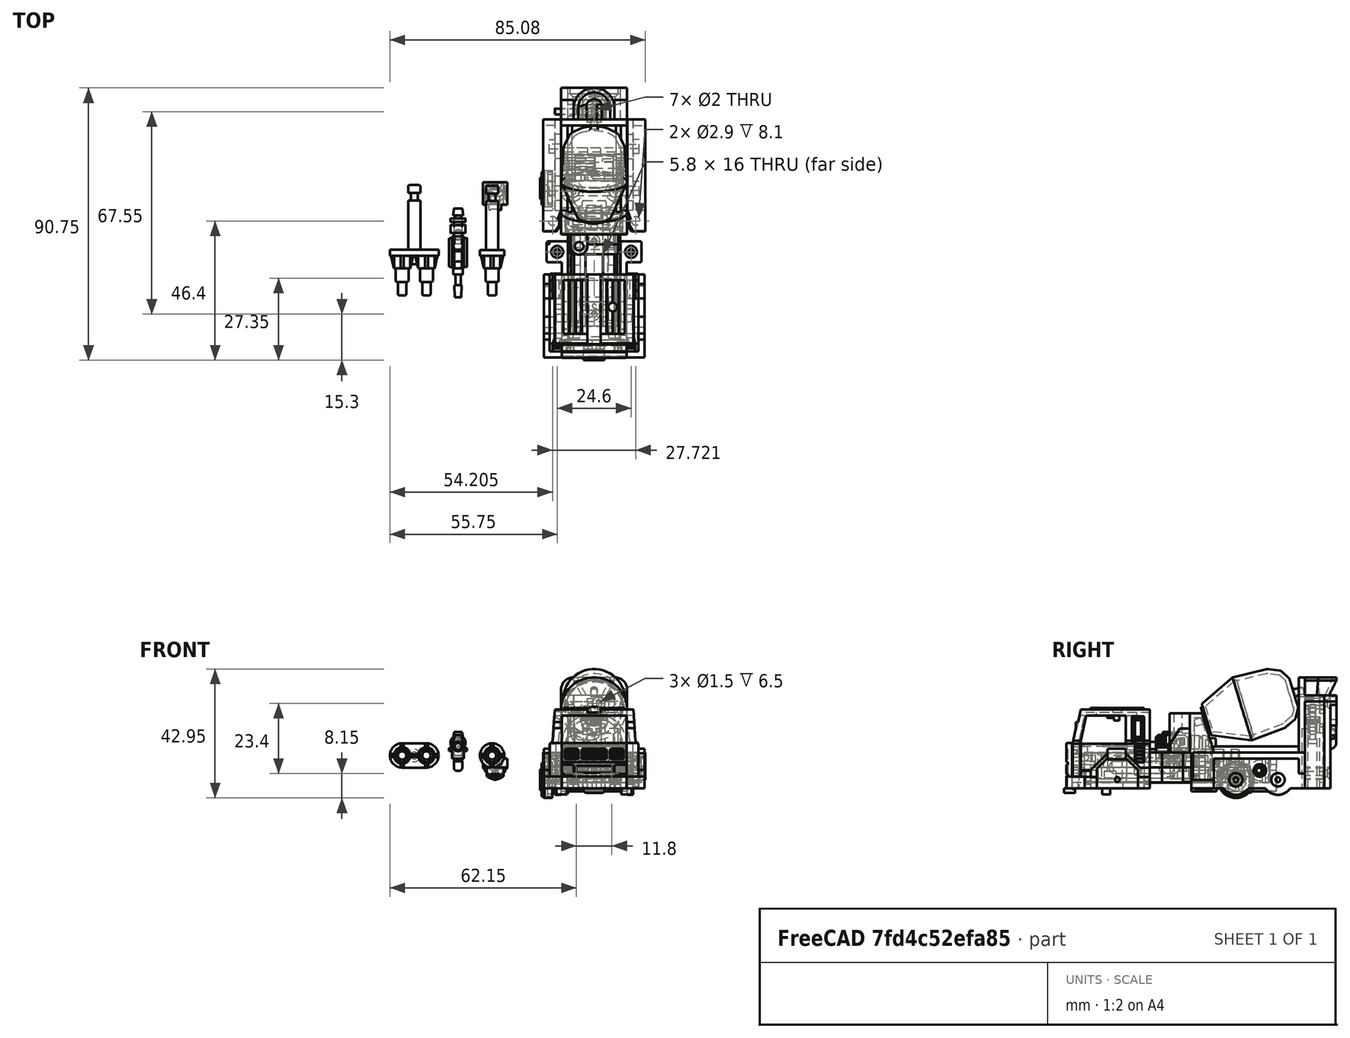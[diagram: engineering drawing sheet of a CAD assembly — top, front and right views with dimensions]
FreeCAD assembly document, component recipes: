
FREECAD ASSEMBLY — COMPONENT RECIPES ("MixMaster")

This assembly document has 25 components, labeled P0..P24 below (a component is one placed body or linked part). 24 of them carry a construction recipe — the FreeCAD feature program that regenerates the part from scratch, quoted from this document or its linked companion documents; the rest are supplied as boundary geometry only. No exploded tour is included for this assembly.
NOTE — this tour is split across 4 documents so each fits a 32k-token context. This is document 1: the component sections continue in the remaining 3 documents, each repeating the header above.
COMPONENT P0 — recipe-attached ("Rear_Torso", modeled in this document).
Construction recipe (the document's own serialized feature program — sketch geometry with constraints, then the solid features built on it; lengths are millimeters unless a unit is written):

FEATURE [Sketcher::SketchObject] Sketch
  ArcFitTolerance = 1e-06
  AttachmentSupport = -> [YZ_Plane]
  FullyConstrained = true
  MakeInternals = false
  MapMode = 5
  Placement = pos=(0,0,0) rot=(0.57735,0.57735,0.57735;2.0944rad)
  sketch-geometry (4):
    g0: LineSegment StartX=-14.5 StartY=1 StartZ=0 EndX=-14.5 EndY=-1 EndZ=0
    g1: LineSegment StartX=-14.5 StartY=-1 StartZ=0 EndX=14.5 EndY=-1 EndZ=0
    g2: LineSegment StartX=14.5 StartY=-1 StartZ=0 EndX=14.5 EndY=1 EndZ=0
    g3: LineSegment StartX=14.5 StartY=1 StartZ=0 EndX=-14.5 EndY=1 EndZ=0
  constraints (12):
    c: Coincident(g0,g1)
    c: Coincident(g1,g2)
    c: Coincident(g2,g3)
    c: Coincident(g3,g0)
    c: Vertical(g0)
    c: Vertical(g2)
    c: Horizontal(g1)
    c: Horizontal(g3)
    c: DistanceX(g3,g3) = 29
    c: DistanceY(g0,g0) = 2
    c: DistanceY(g-1,g0) = 1
    c: DistanceX(g0,g-1) = 14.5
FEATURE [PartDesign::Pad] Pad
  Direction = (1,0,0)
  Length = 22
  Length2 = 10
  Placement = pos=(0,0,0) rot=(1,1,1;2.0944rad)
  Profile = -> Sketch
  ReferenceAxis = -> Sketch [N_Axis]
  Refine = true
  Suppressed = false
  Type = 0
FEATURE [Sketcher::SketchObject] Sketch001
  ArcFitTolerance = 1e-06
  AttachmentSupport = -> [Pad]
  ExternalGeometry = -> [Pad]
  FullyConstrained = true
  MakeInternals = false
  MapMode = 5
  Placement = pos=(22,0,0) rot=(0.57735,0.57735,0.57735;2.0944rad)
  sketch-geometry (4):
    g0: LineSegment StartX=-14.5 StartY=1 StartZ=0 EndX=-21.3 EndY=1 EndZ=0
    g1: LineSegment StartX=-21.3 StartY=1 StartZ=0 EndX=-21.3 EndY=-6 EndZ=0
    g2: LineSegment StartX=-21.3 StartY=-6 StartZ=0 EndX=-14.5 EndY=-6 EndZ=0
    g3: LineSegment StartX=-14.5 StartY=-6 StartZ=0 EndX=-14.5 EndY=1 EndZ=0
  constraints (11):
    c: Coincident(g0,g1)
    c: Coincident(g1,g2)
    c: Coincident(g2,g3)
    c: Coincident(g3,g0)
    c: Horizontal(g0)
    c: Horizontal(g2)
    c: Vertical(g1)
    c: Vertical(g3)
    c: Coincident(g0,g-3)
    c: DistanceX(g0,g0) = 6.8
    c: DistanceY(g1,g1) = 7
FEATURE [PartDesign::Pad] Pad001
  BaseFeature = -> Pad
  Direction = (1,0,0)
  Length = 1.5
  Length2 = 10
  Placement = pos=(0,0,0) rot=(1,1,1;2.0944rad)
  Profile = -> Sketch001
  ReferenceAxis = -> Sketch001 [N_Axis]
  Refine = true
  Reversed = true
  Suppressed = false
  Type = 0
FEATURE [Sketcher::SketchObject] Sketch002
  ArcFitTolerance = 1e-06
  AttachmentSupport = -> [Pad001]
  ExternalGeometry = -> [Pad001]
  FullyConstrained = true
  MakeInternals = false
  MapMode = 5
  Placement = pos=(22,0,0) rot=(0.57735,0.57735,0.57735;2.0944rad)
  sketch-geometry (4):
    g0: LineSegment StartX=-21.8 StartY=1 StartZ=0 EndX=-13.8 EndY=1 EndZ=0
    g1: LineSegment StartX=-13.8 StartY=1 StartZ=0 EndX=-17.8 EndY=14.1 EndZ=0
    g2: LineSegment StartX=-17.8 StartY=14.1 StartZ=0 EndX=-21.8 EndY=14.1 EndZ=0
    g3: LineSegment StartX=-21.8 StartY=14.1 StartZ=0 EndX=-21.8 EndY=1 EndZ=0
  constraints (12):
    c: Coincident(g0,g1)
    c: Coincident(g1,g2)
    c: Coincident(g2,g3)
    c: Horizontal(g0)
    c: Horizontal(g2)
    c: DistanceY(g3,g3) = 13.1
    c: DistanceX(g0,g0) = 8
    c: Coincident(g0,g3)
    c: Vertical(g3)
    c: DistanceX(g0,g-3) = 0.5
    c: DistanceX(g2,g2) = 4
    c: PointOnObject(g-3,g0)
FEATURE [PartDesign::Pad] Pad002
  BaseFeature = -> Pad001
  Direction = (1,0,0)
  Length = 22
  Length2 = 10
  Placement = pos=(0,0,0) rot=(1,1,1;2.0944rad)
  Profile = -> Sketch002
  ReferenceAxis = -> Sketch002 [N_Axis]
  Refine = true
  Reversed = true
  Suppressed = false
  Type = 0
FEATURE [Sketcher::SketchObject] Sketch003
  ArcFitTolerance = 1e-06
  AttachmentSupport = -> [Pad002]
  ExternalGeometry = -> [Pad002]
  FullyConstrained = true
  MakeInternals = false
  MapMode = 5
  Placement = pos=(8e-16,0,0) rot=(0.57735,0.57735,-0.57735;4.18879rad)
  sketch-geometry (4):
    g0: LineSegment StartX=-14.5 StartY=-1 StartZ=0 EndX=-14.5 EndY=6 EndZ=0
    g1: LineSegment StartX=-14.5 StartY=6 StartZ=0 EndX=-21.3 EndY=6 EndZ=0
    g2: LineSegment StartX=-21.3 StartY=6 StartZ=0 EndX=-21.3 EndY=-1 EndZ=0
    g3: LineSegment StartX=-21.3 StartY=-1 StartZ=0 EndX=-14.5 EndY=-1 EndZ=0
  constraints (11):
    c: Coincident(g0,g1)
    c: Coincident(g1,g2)
    c: Coincident(g2,g3)
    c: Coincident(g3,g0)
    c: Vertical(g0)
    c: Vertical(g2)
    c: Horizontal(g1)
    c: Horizontal(g3)
    c: Coincident(g0,g-4)
    c: DistanceX(g1,g1) = 6.8
    c: DistanceY(g0,g0) = 7
FEATURE [PartDesign::Pad] Pad003
  BaseFeature = -> Pad002
  Direction = (-1,0,0)
  Length = 1.5
  Length2 = 10
  Placement = pos=(0,0,0) rot=(1,1,1;2.0944rad)
  Profile = -> Sketch003
  ReferenceAxis = -> Sketch003 [N_Axis]
  Refine = true
  Reversed = true
  Suppressed = false
  Type = 0
FEATURE [Sketcher::SketchObject] Sketch004
  ArcFitTolerance = 1e-06
  AttachmentSupport = -> [Pad003]
  ExternalGeometry = -> [Pad003]
  FullyConstrained = true
  MakeInternals = false
  MapMode = 5
  Placement = pos=(-4.8e-15,-21.8,0) rot=(0.57735,0.57735,-0.57735;2.0944rad)
  sketch-geometry (4):
    g0: ArcOfCircle CenterX=-3.1 CenterY=11 CenterZ=0 NormalX=0 NormalY=0 NormalZ=1 AngleXU=0 Radius=11 StartAngle=1.5708 EndAngle=4.71239
    g1: LineSegment StartX=-3.1 StartY=22 StartZ=0 EndX=-14.1 EndY=22 EndZ=0
    g2: LineSegment StartX=-14.1 StartY=22 StartZ=0 EndX=-14.1 EndY=0 EndZ=0
    g3: LineSegment StartX=-14.1 StartY=0 StartZ=0 EndX=-3.1 EndY=0 EndZ=0
  constraints (10):
    c: PointOnObject(g0,g-1)
    c: PointOnObject(g0,g-3)
    c: DistanceX(g0,g0) = 0
    c: DistanceX(g0,g-5) = 2.1
    c: Tangent(g1,g0) = -1.5708
    c: Coincident(g1,g-4)
    c: Coincident(g2,g1)
    c: Coincident(g2,g-4)
    c: Coincident(g3,g2)
    c: Coincident(g3,g0)
FEATURE [PartDesign::Pocket] Pocket
  BaseFeature = -> Pad003
  Direction = (0,1,0)
  Length = 8
  Length2 = 5
  Placement = pos=(0,0,0) rot=(1,1,1;2.0944rad)
  Profile = -> Sketch004
  ReferenceAxis = -> Sketch004 [N_Axis]
  Refine = true
  Suppressed = false
  Type = 0
FEATURE [Sketcher::SketchObject] Sketch005
  ArcFitTolerance = 1e-06
  AttachmentSupport = -> [Pocket]
  ExternalGeometry = -> [Pocket]
  FullyConstrained = true
  MakeInternals = false
  MapMode = 5
  Placement = pos=(-4.8e-15,-21.8,0) rot=(0.57735,0.57735,-0.57735;2.0944rad)
  sketch-geometry (4):
    g0: ArcOfCircle CenterX=-3.1 CenterY=11 CenterZ=0 NormalX=0 NormalY=0 NormalZ=1 AngleXU=0 Radius=9.5 StartAngle=1.5708 EndAngle=4.71239
    g1: LineSegment StartX=-3.1 StartY=20.5 StartZ=0 EndX=-1 EndY=20.5 EndZ=0
    g2: LineSegment StartX=-3.1 StartY=1.5 StartZ=0 EndX=-1 EndY=1.5 EndZ=0
    g3: LineSegment StartX=-1 StartY=20.5 StartZ=0 EndX=-1 EndY=1.5 EndZ=0
  constraints (12):
    c: Coincident(g0,g-3)
    c: Radius(g0) = 9.5
    c: Coincident(g1,g0)
    c: PointOnObject(g1,g-4)
    c: Horizontal(g1)
    c: Coincident(g2,g0)
    c: PointOnObject(g2,g-4)
    c: Horizontal(g2)
    c: DistanceY(g0,g-5) = 1.5
    c: DistanceX(g0,g0) = 0
    c: Coincident(g3,g1)
    c: Coincident(g3,g2)
FEATURE [Sketcher::SketchObject] Sketch006
  ArcFitTolerance = 1e-06
  FullyConstrained = true
  MakeInternals = false
  MapMode = 5
  Placement = pos=(1.4e-15,-12.3438,-3.7691) rot=(-0.511311,-0.511311,-0.690741;1.93262rad)
  sketch-geometry (4):
    g0: ArcOfCircle CenterX=7.18218 CenterY=11 CenterZ=0 NormalX=0 NormalY=0 NormalZ=1 AngleXU=0 Radius=9.5 StartAngle=4.71239 EndAngle=7.85398
    g1: LineSegment StartX=7.18218 StartY=1.5 StartZ=0 EndX=4.98646 EndY=1.5 EndZ=0
    g2: LineSegment StartX=7.18218 StartY=20.5 StartZ=0 EndX=4.98646 EndY=20.5 EndZ=0
    g3: LineSegment StartX=4.98646 StartY=20.5 StartZ=0 EndX=4.98646 EndY=1.5 EndZ=0
  constraints (12):
    c: Coincident(g0,g-3)
    c: Radius(g0) = 9.5
    c: Coincident(g1,g0)
    c: PointOnObject(g1,g-5)
    c: Horizontal(g1)
    c: Coincident(g2,g0)
    c: PointOnObject(g2,g-5)
    c: Horizontal(g2)
    c: Coincident(g3,g2)
    c: Coincident(g3,g1)
    c: DistanceX(g0,g0) = 0
    c: DistanceX(g0,g0) = 0
FEATURE [PartDesign::Pocket] Pocket002
  BaseFeature = -> Pocket
  Direction = (-1e-16,-0.956408,-0.292033)
  Length = 8
  Length2 = 5
  Placement = pos=(0,0,0) rot=(1,1,1;2.0944rad)
  Profile = -> Sketch006
  ReferenceAxis = -> Sketch006 [N_Axis]
  Refine = true
  Suppressed = false
  Type = 0
FEATURE [PartDesign::Pocket] Pocket003
  BaseFeature = -> Pocket002
  Direction = (0,1,0)
  Length = 8
  Length2 = 5
  Placement = pos=(0,0,0) rot=(1,1,1;2.0944rad)
  Profile = -> Sketch005
  ReferenceAxis = -> Sketch005 [N_Axis]
  Refine = true
  Suppressed = false
  Type = 0
FEATURE [Sketcher::SketchObject] Sketch007
  ArcFitTolerance = 1e-06
  AttachmentSupport = -> [Pocket003]
  ExternalGeometry = -> [Pocket003]
  FullyConstrained = true
  MakeInternals = false
  MapMode = 5
  Placement = pos=(-2.7e-15,-12.3438,-3.7691) rot=(-0.511311,-0.511311,-0.690741;1.93262rad)
  sketch-geometry (4):
    g0: LineSegment StartX=7.18218 StartY=21 StartZ=0 EndX=4.98646 EndY=21 EndZ=0
    g1: LineSegment StartX=4.98646 StartY=21 StartZ=0 EndX=4.98646 EndY=1 EndZ=0
    g2: LineSegment StartX=4.98646 StartY=1 StartZ=0 EndX=7.18218 EndY=1 EndZ=0
    g3: ArcOfCircle CenterX=7.18218 CenterY=11 CenterZ=0 NormalX=0 NormalY=0 NormalZ=1 AngleXU=0 Radius=10 StartAngle=4.71239 EndAngle=7.85398
  constraints (12):
    c: Vertical(g1)
    c: Horizontal(g2)
    c: PointOnObject(g2,g-6)
    c: Coincident(g2,g3)
    c: Coincident(g0,g3)
    c: Horizontal(g0)
    c: Radius(g3) = 10
    c: Coincident(g-3,g3)
    c: DistanceX(g0,g3) = 0
    c: DistanceX(g2,g3) = 0
    c: Coincident(g1,g2)
    c: Coincident(g1,g0)
FEATURE [PartDesign::Pad] Pad004
  BaseFeature = -> Pocket003
  Direction = (0,0.956408,0.292033)
  Length = 0.734
  Length2 = 10
  Placement = pos=(0,0,0) rot=(1,1,1;2.0944rad)
  Profile = -> Sketch007
  ReferenceAxis = -> Sketch007 [N_Axis]
  Refine = true
  Reversed = true
  Suppressed = false
  Type = 0
FEATURE [Sketcher::SketchObject] Sketch008
  ArcFitTolerance = 1e-06
  AttachmentSupport = -> [Pad004]
  ExternalGeometry = -> [Pad004]
  FullyConstrained = true
  MakeInternals = false
  MapMode = 5
  Placement = pos=(22,0,1.47e-14) rot=(0.57735,0.57735,0.57735;2.0944rad)
  sketch-geometry (4):
    g0: LineSegment StartX=14.5 StartY=26 StartZ=0 EndX=14.5 EndY=-11 EndZ=0
    g1: LineSegment StartX=14.5 StartY=-11 StartZ=0 EndX=16.5 EndY=-11 EndZ=0
    g2: LineSegment StartX=16.5 StartY=-11 StartZ=0 EndX=16.5 EndY=26 EndZ=0
    g3: LineSegment StartX=16.5 StartY=26 StartZ=0 EndX=14.5 EndY=26 EndZ=0
  constraints (12):
    c: Coincident(g0,g1)
    c: Coincident(g1,g2)
    c: Coincident(g2,g3)
    c: Coincident(g3,g0)
    c: Vertical(g0)
    c: Vertical(g2)
    c: Horizontal(g1)
    c: Horizontal(g3)
    c: DistanceY(g2,g2) = 37
    c: DistanceX(g3,g3) = 2
    c: PointOnObject(g-3,g0)
    c: DistanceY(g0,g-3) = 10
FEATURE [PartDesign::Pad] Pad005
  BaseFeature = -> Pad004
  Direction = (1,-1e-15,1.2e-15)
  Length = 22
  Length2 = 10
  Placement = pos=(0,0,0) rot=(1,1,1;2.0944rad)
  Profile = -> Sketch008
  ReferenceAxis = -> Sketch008 [N_Axis]
  Refine = true
  Reversed = true
  Suppressed = false
  Type = 0
FEATURE [Sketcher::SketchObject] Sketch009
  ArcFitTolerance = 1e-06
  AttachmentSupport = -> [Pad005]
  ExternalGeometry = -> [Pad005]
  FullyConstrained = true
  MakeInternals = false
  MapMode = 5
  Placement = pos=(-1.21e-14,-12.3438,-3.7691) rot=(-0.511311,-0.511311,-0.690741;1.93262rad)
  sketch-geometry (4):
    g0: LineSegment StartX=14.4865 StartY=12.3 StartZ=0 EndX=14.4865 EndY=9.7 EndZ=0
    g1: LineSegment StartX=14.4865 StartY=9.7 StartZ=0 EndX=17.0865 EndY=9.7 EndZ=0
    g2: LineSegment StartX=17.0865 StartY=9.7 StartZ=0 EndX=17.0865 EndY=12.3 EndZ=0
    g3: LineSegment StartX=17.0865 StartY=12.3 StartZ=0 EndX=14.4865 EndY=12.3 EndZ=0
  constraints (12):
    c: Coincident(g0,g1)
    c: Coincident(g1,g2)
    c: Coincident(g2,g3)
    c: Coincident(g3,g0)
    c: Vertical(g0)
    c: Vertical(g2)
    c: Horizontal(g1)
    c: Horizontal(g3)
    c: DistanceX(g3,g3) = 2.6
    c: DistanceY(g0,g0) = 2.6
    c: DistanceX(g-3,g0) = 9.5
    c: DistanceY(g0,g-3) = 9.7
FEATURE [PartDesign::Pocket] Pocket004
  BaseFeature = -> Pad005
  Direction = (0,-0.956408,-0.292033)
  Length = 1
  Length2 = 5
  Placement = pos=(0,0,0) rot=(1,1,1;2.0944rad)
  Profile = -> Sketch009
  ReferenceAxis = -> Sketch009 [N_Axis]
  Refine = true
  Suppressed = false
  Type = 0
FEATURE [Sketcher::SketchObject] Sketch010
  ArcFitTolerance = 1e-06
  AttachmentSupport = -> [Pocket004]
  ExternalGeometry = -> [Pocket004]
  FullyConstrained = true
  MakeInternals = false
  MapMode = 5
  Placement = pos=(0,5e-16,1) rot=(0,0,-1;1.5708rad)
  sketch-geometry (8):
    g0: LineSegment StartX=-14.5 StartY=19.9 StartZ=0 EndX=-14.5 EndY=18.3 EndZ=0
    g1: LineSegment StartX=-14.5 StartY=18.3 StartZ=0 EndX=14.502 EndY=18.3 EndZ=0
    g2: LineSegment StartX=14.502 StartY=18.3 StartZ=0 EndX=14.502 EndY=19.9 EndZ=0
    g3: LineSegment StartX=14.502 StartY=19.9 StartZ=0 EndX=-14.5 EndY=19.9 EndZ=0
    g4: LineSegment StartX=-14.5 StartY=3.7 StartZ=0 EndX=-14.5 EndY=2.1 EndZ=0
    g5: LineSegment StartX=-14.5 StartY=2.1 StartZ=0 EndX=14.502 EndY=2.1 EndZ=0
    g6: LineSegment StartX=14.502 StartY=2.1 StartZ=0 EndX=14.502 EndY=3.7 EndZ=0
    g7: LineSegment StartX=14.502 StartY=3.7 StartZ=0 EndX=-14.5 EndY=3.7 EndZ=0
  constraints (24):
    c: Coincident(g0,g1)
    c: Coincident(g1,g2)
    c: Coincident(g2,g3)
    c: Coincident(g3,g0)
    c: Vertical(g0)
    c: Horizontal(g1)
    c: Horizontal(g3)
    c: PointOnObject(g0,g-4)
    c: Coincident(g4,g5)
    c: Coincident(g5,g6)
    c: Coincident(g7,g4)
    c: Vertical(g4)
    c: Horizontal(g5)
    c: Horizontal(g7)
    c: PointOnObject(g4,g-4)
    c: DistanceY(g4,g4) = 1.6
    c: DistanceY(g0,g0) = 1.6
    c: DistanceY(g0,g-5) = 2.1
    c: DistanceY(g-6,g4) = 2.1
    c: PointOnObject(g7,g-7)
    c: Coincident(g6,g7)
    c: PointOnObject(g5,g-7)
    c: PointOnObject(g2,g-7)
    c: PointOnObject(g1,g-7)
FEATURE [PartDesign::Pad] Pad006
  BaseFeature = -> Pocket004
  Direction = (-2.8e-15,1.5e-15,1)
  Length = 2
  Length2 = 10
  Placement = pos=(0,0,0) rot=(1,1,1;2.0944rad)
  Profile = -> Sketch010
  ReferenceAxis = -> Sketch010 [N_Axis]
  Refine = true
  Suppressed = false
  Type = 0
FEATURE [Sketcher::SketchObject] Sketch011
  ArcFitTolerance = 1e-06
  AttachmentSupport = -> [Pad006]
  ExternalGeometry = -> [Pad006]
  FullyConstrained = true
  MakeInternals = false
  MapMode = 5
  Placement = pos=(1.77e-14,14.5,1.6e-15) rot=(0.57735,0.57735,-0.57735;2.0944rad)
  sketch-geometry (6):
    g0: LineSegment StartX=-26 StartY=22 StartZ=0 EndX=-22 EndY=22 EndZ=0
    g1: LineSegment StartX=-26 StartY=22 StartZ=0 EndX=-26 EndY=18 EndZ=0
    g2: ArcOfCircle CenterX=-22 CenterY=18 CenterZ=0 NormalX=0 NormalY=0 NormalZ=1 AngleXU=0 Radius=4 StartAngle=1.5708 EndAngle=3.14159
    g3: LineSegment StartX=-26 StartY=0 StartZ=0 EndX=-26 EndY=4 EndZ=0
    g4: LineSegment StartX=-26 StartY=0 StartZ=0 EndX=-22 EndY=-4e-15 EndZ=0
    g5: ArcOfCircle CenterX=-22 CenterY=4 CenterZ=0 NormalX=0 NormalY=0 NormalZ=1 AngleXU=0 Radius=4 StartAngle=3.14159 EndAngle=4.71239
  constraints (18):
    c: Coincident(g0,g-4)
    c: PointOnObject(g0,g-3)
    c: Coincident(g1,g0)
    c: PointOnObject(g1,g-4)
    c: Coincident(g2,g1)
    c: Coincident(g2,g0)
    c: Coincident(g3,g-5)
    c: PointOnObject(g3,g-4)
    c: Coincident(g4,g3)
    c: PointOnObject(g4,g-5)
    c: Coincident(g5,g4)
    c: Coincident(g5,g3)
    c: Radius(g5) = 4
    c: Radius(g2) = 4
    c: DistanceX(g5,g4) = 0
    c: DistanceX(g0,g2) = 0
    c: DistanceY(g1,g2) = 0
    c: DistanceY(g3,g5) = 0
FEATURE [PartDesign::Pocket] Pocket005
  BaseFeature = -> Pad006
  Direction = (1.3e-15,1,0)
  Length = 2
  Length2 = 5
  Placement = pos=(0,0,0) rot=(1,1,1;2.0944rad)
  Profile = -> Sketch011
  ReferenceAxis = -> Sketch011 [N_Axis]
  Refine = true
  Suppressed = false
  Type = 0
FEATURE [Sketcher::SketchObject] Sketch012
  ArcFitTolerance = 1e-06
  AttachmentSupport = -> [Pocket005]
  ExternalGeometry = -> [Pocket005]
  FullyConstrained = true
  MakeInternals = false
  MapMode = 5
  Placement = pos=(1.77e-14,14.5,1.6e-15) rot=(0.57735,0.57735,-0.57735;2.0944rad)
  sketch-geometry (4):
    g0: LineSegment StartX=-21.9 StartY=12.1 StartZ=0 EndX=-21.9 EndY=9.9 EndZ=0
    g1: LineSegment StartX=-21.9 StartY=9.9 StartZ=0 EndX=-19.1 EndY=9.9 EndZ=0
    g2: LineSegment StartX=-19.1 StartY=9.9 StartZ=0 EndX=-19.1 EndY=12.1 EndZ=0
    g3: LineSegment StartX=-19.1 StartY=12.1 StartZ=0 EndX=-21.9 EndY=12.1 EndZ=0
  constraints (12):
    c: Coincident(g0,g1)
    c: Coincident(g1,g2)
    c: Coincident(g2,g3)
    c: Coincident(g3,g0)
    c: Vertical(g0)
    c: Vertical(g2)
    c: Horizontal(g1)
    c: Horizontal(g3)
    c: DistanceX(g3,g3) = 2.8
    c: DistanceY(g0,g0) = 2.2
    c: DistanceY(g0,g-3) = 9.9
    c: DistanceX(g-5,g0) = 4.1
FEATURE [PartDesign::Pocket] Pocket006
  BaseFeature = -> Pocket005
  Direction = (1.3e-15,1,0)
  Length = 2
  Length2 = 5
  Placement = pos=(0,0,0) rot=(1,1,1;2.0944rad)
  Profile = -> Sketch012
  ReferenceAxis = -> Sketch012 [N_Axis]
  Refine = true
  Suppressed = false
  Type = 0
FEATURE [Sketcher::SketchObject] Sketch015
  ArcFitTolerance = 1e-06
  AttachmentSupport = -> [Pocket006]
  ExternalGeometry = -> [Pocket006]
  FullyConstrained = true
  MakeInternals = false
  MapMode = 5
  Placement = pos=(-4.8e-15,-21.8,0) rot=(0.57735,0.57735,-0.57735;2.0944rad)
  sketch-geometry (4):
    g0: LineSegment StartX=-1 StartY=20.5 StartZ=0 EndX=-1 EndY=1.5 EndZ=0
    g1: LineSegment StartX=-1 StartY=1.5 StartZ=0 EndX=-3.1 EndY=1.5 EndZ=0
    g2: LineSegment StartX=-1 StartY=20.5 StartZ=0 EndX=-3.1 EndY=20.5 EndZ=0
    g3: ArcOfCircle CenterX=-3.1 CenterY=11 CenterZ=0 NormalX=0 NormalY=0 NormalZ=1 AngleXU=0 Radius=9.5 StartAngle=1.5708 EndAngle=4.71239
  constraints (9):
    c: Coincident(g0,g-3)
    c: Coincident(g0,g-4)
    c: Coincident(g1,g0)
    c: Coincident(g1,g-5)
    c: Coincident(g2,g0)
    c: Coincident(g2,g-5)
    c: Coincident(g3,g2)
    c: Coincident(g3,g1)
    c: Radius(g3) = 9.5
FEATURE [PartDesign::Pad] Pad007
  BaseFeature = -> Pocket006
  Direction = (-1e-16,-1,3.2e-15)
  Length = 1.5
  Length2 = 10
  Placement = pos=(0,0,0) rot=(1,1,1;2.0944rad)
  Profile = -> Sketch015
  ReferenceAxis = -> Sketch015 [N_Axis]
  Refine = true
  Reversed = true
  Suppressed = false
  Type = 0
FEATURE [Sketcher::SketchObject] Sketch016
  ArcFitTolerance = 1e-06
  AttachmentSupport = -> [Pad007]
  ExternalGeometry = -> [Pad007]
  FullyConstrained = true
  MakeInternals = false
  MapMode = 5
  Placement = pos=(-3.62e-14,-21.8,8.98e-14) rot=(0.57735,0.57735,-0.57735;2.0944rad)
  sketch-geometry (4):
    g0: LineSegment StartX=-1 StartY=4.5 StartZ=0 EndX=-7.5 EndY=4.5 EndZ=0
    g1: LineSegment StartX=-7.5 StartY=4.5 StartZ=0 EndX=-7.5 EndY=17.5 EndZ=0
    g2: LineSegment StartX=-7.5 StartY=17.5 StartZ=0 EndX=-1 EndY=17.5 EndZ=0
    g3: LineSegment StartX=-1 StartY=17.5 StartZ=0 EndX=-1 EndY=4.5 EndZ=0
  constraints (12):
    c: PointOnObject(g0,g-3)
    c: Horizontal(g0)
    c: Coincident(g1,g0)
    c: Vertical(g1)
    c: Coincident(g2,g1)
    c: PointOnObject(g2,g-3)
    c: Horizontal(g2)
    c: Coincident(g3,g2)
    c: Coincident(g3,g0)
    c: DistanceY(g-3,g0) = 4.5
    c: DistanceY(g2,g-3) = 4.5
    c: DistanceX(g2,g2) = 6.5
FEATURE [PartDesign::Pocket] Pocket007
  BaseFeature = -> Pad007
  Direction = (1.6e-15,1,-4.3e-15)
  Length = 1.5
  Length2 = 5
  Placement = pos=(0,0,0) rot=(1,1,1;2.0944rad)
  Profile = -> Sketch016
  ReferenceAxis = -> Sketch016 [N_Axis]
  Refine = true
  Suppressed = false
  Type = 0
FEATURE [Sketcher::SketchObject] Sketch017
  ArcFitTolerance = 1e-06
  AttachmentSupport = -> [Pocket007]
  ExternalGeometry = -> [Pocket007]
  FullyConstrained = true
  MakeInternals = false
  MapMode = 5
  Placement = pos=(-3.62e-14,-21.8,8.98e-14) rot=(0.57735,0.57735,-0.57735;2.0944rad)
  sketch-geometry (8):
    g0: LineSegment StartX=-1 StartY=4.5 StartZ=0 EndX=-7.5 EndY=4.5 EndZ=0
    g1: LineSegment StartX=-7.5 StartY=17.5 StartZ=0 EndX=-7.5 EndY=4.5 EndZ=0
    g2: LineSegment StartX=-7.5 StartY=17.5 StartZ=0 EndX=-1 EndY=17.5 EndZ=0
    g3: LineSegment StartX=-1 StartY=17.5 StartZ=0 EndX=-1 EndY=19 EndZ=0
    g4: LineSegment StartX=-1 StartY=19 StartZ=0 EndX=-9 EndY=19 EndZ=0
    g5: LineSegment StartX=-9 StartY=19 StartZ=0 EndX=-9 EndY=3 EndZ=0
    g6: LineSegment StartX=-9 StartY=3 StartZ=0 EndX=-1 EndY=3 EndZ=0
    g7: LineSegment StartX=-1 StartY=3 StartZ=0 EndX=-1 EndY=4.5 EndZ=0
  constraints (20):
    c: Coincident(g0,g-5)
    c: Coincident(g0,g-5)
    c: Coincident(g1,g-4)
    c: Coincident(g1,g0)
    c: Coincident(g2,g1)
    c: Coincident(g2,g-3)
    c: Coincident(g3,g2)
    c: Vertical(g3)
    c: Coincident(g4,g3)
    c: Horizontal(g4)
    c: Coincident(g5,g4)
    c: Vertical(g5)
    c: Coincident(g6,g5)
    c: Horizontal(g6)
    c: Coincident(g7,g6)
    c: Coincident(g7,g0)
    c: Vertical(g7)
    c: DistanceY(g3,g3) = 1.5
    c: DistanceY(g7,g7) = 1.5
    c: DistanceX(g5,g0) = 1.5
FEATURE [PartDesign::Pad] Pad008
  BaseFeature = -> Pocket007
  Direction = (-1.8e-15,-1,4.5e-15)
  Length = 3.3
  Length2 = 10
  Placement = pos=(0,0,0) rot=(1,1,1;2.0944rad)
  Profile = -> Sketch017
  ReferenceAxis = -> Sketch017 [N_Axis]
  Refine = true
  Suppressed = false
  Type = 0
FEATURE [Sketcher::SketchObject] Sketch018
  ArcFitTolerance = 1e-06
  AttachmentSupport = -> [Pad008]
  ExternalGeometry = -> [Pad008]
  FullyConstrained = true
  MakeInternals = false
  MapMode = 5
  Placement = pos=(3,-5.5e-15,-7e-16) rot=(-0.57735,-0.57735,0.57735;2.0944rad)
  sketch-geometry (4):
    g0: LineSegment StartX=-25.1 StartY=-1 StartZ=0 EndX=-25.1 EndY=-9 EndZ=0
    g1: LineSegment StartX=-25.1 StartY=-9 StartZ=0 EndX=-28.4 EndY=-4 EndZ=0
    g2: LineSegment StartX=-28.4 StartY=-4 StartZ=0 EndX=-28.4 EndY=-1 EndZ=0
    g3: LineSegment StartX=-25.1 StartY=-1 StartZ=0 EndX=-28.4 EndY=-1 EndZ=0
  constraints (10):
    c: Coincident(g0,g-3)
    c: Coincident(g0,g-3)
    c: Coincident(g1,g0)
    c: Coincident(g2,g1)
    c: Vertical(g2)
    c: Coincident(g3,g0)
    c: Horizontal(g3)
    c: Coincident(g3,g2)
    c: DistanceX(g3,g3) = 3.3
    c: DistanceY(g2,g2) = 3
FEATURE [PartDesign::Pad] Pad009
  BaseFeature = -> Pad008
  Direction = (-1,1.8e-15,0)
  Length = 1.5
  Length2 = 10
  Placement = pos=(0,0,0) rot=(1,1,1;2.0944rad)
  Profile = -> Sketch018
  ReferenceAxis = -> Sketch018 [N_Axis]
  Refine = true
  Reversed = true
  Suppressed = false
  Type = 0
FEATURE [Sketcher::SketchObject] Sketch019
  ArcFitTolerance = 1e-06
  AttachmentSupport = -> [Pad009]
  ExternalGeometry = -> [Pad009]
  FullyConstrained = true
  MakeInternals = false
  MapMode = 5
  Placement = pos=(19,-3.48e-14,-4.2e-15) rot=(0.57735,0.57735,0.57735;2.0944rad)
  sketch-geometry (4):
    g0: LineSegment StartX=-25.1 StartY=9 StartZ=0 EndX=-25.1 EndY=1 EndZ=0
    g1: LineSegment StartX=-25.1 StartY=1 StartZ=0 EndX=-28.4 EndY=1 EndZ=0
    g2: LineSegment StartX=-28.4 StartY=1 StartZ=0 EndX=-28.4 EndY=4 EndZ=0
    g3: LineSegment StartX=-28.4 StartY=4 StartZ=0 EndX=-25.1 EndY=9 EndZ=0
  constraints (10):
    c: Coincident(g0,g-3)
    c: Coincident(g0,g-3)
    c: Coincident(g1,g0)
    c: Horizontal(g1)
    c: Coincident(g2,g1)
    c: Vertical(g2)
    c: Coincident(g3,g2)
    c: Coincident(g3,g0)
    c: DistanceX(g1,g1) = 3.3
    c: DistanceY(g2,g2) = 3
FEATURE [PartDesign::Pad] Pad010
  BaseFeature = -> Pad009
  Direction = (1,-1.9e-15,-1e-16)
  Length = 1.5
  Length2 = 10
  Placement = pos=(0,0,0) rot=(1,1,1;2.0944rad)
  Profile = -> Sketch019
  ReferenceAxis = -> Sketch019 [N_Axis]
  Refine = true
  Reversed = true
  Suppressed = false
  Type = 0
FEATURE [Sketcher::SketchObject] Sketch020
  ArcFitTolerance = 1e-06
  AttachmentSupport = -> [Pad010]
  ExternalGeometry = -> [Pad010]
  FullyConstrained = true
  MakeInternals = false
  MapMode = 5
  Placement = pos=(-4.33e-14,-21.6216,14.2703) rot=(0.428244,0.428244,-0.795748;1.79731rad)
  sketch-geometry (4):
    g0: LineSegment StartX=12.3055 StartY=17.5 StartZ=0 EndX=6.31465 EndY=17.5 EndZ=0
    g1: LineSegment StartX=6.31465 StartY=17.5 StartZ=0 EndX=6.31465 EndY=4.5 EndZ=0
    g2: LineSegment StartX=6.31465 StartY=4.5 StartZ=0 EndX=12.3055 EndY=4.5 EndZ=0
    g3: LineSegment StartX=12.3055 StartY=4.5 StartZ=0 EndX=12.3055 EndY=17.5 EndZ=0
  constraints (8):
    c: Coincident(g0,g-3)
    c: Coincident(g0,g-4)
    c: Coincident(g1,g0)
    c: Coincident(g1,g-5)
    c: Coincident(g2,g1)
    c: Coincident(g2,g-5)
    c: Coincident(g3,g2)
    c: Coincident(g3,g0)
FEATURE [PartDesign::Pad] Pad011
  BaseFeature = -> Pad010
  Direction = (-1.9e-15,-0.834609,0.550842)
  Length = 1.5
  Length2 = 10
  Placement = pos=(0,0,0) rot=(1,1,1;2.0944rad)
  Profile = -> Sketch020
  ReferenceAxis = -> Sketch020 [N_Axis]
  Refine = true
  Reversed = true
  Suppressed = false
  Type = 0
FEATURE [Sketcher::SketchObject] Sketch021
  ArcFitTolerance = 1e-06
  AttachmentSupport = -> [Pad011]
  ExternalGeometry = -> [Pad011]
  FullyConstrained = true
  MakeInternals = false
  MapMode = 5
  Placement = pos=(-5.68e-14,-28.4,0) rot=(0.57735,0.57735,-0.57735;2.0944rad)
  sketch-geometry (4):
    g0: LineSegment StartX=-1 StartY=17.5 StartZ=0 EndX=-4 EndY=17.5 EndZ=0
    g1: LineSegment StartX=-4 StartY=17.5 StartZ=0 EndX=-4 EndY=4.5 EndZ=0
    g2: LineSegment StartX=-4 StartY=4.5 StartZ=0 EndX=-1 EndY=4.5 EndZ=0
    g3: LineSegment StartX=-1 StartY=4.5 StartZ=0 EndX=-1 EndY=17.5 EndZ=0
  constraints (8):
    c: Coincident(g0,g-3)
    c: Coincident(g0,g-4)
    c: Coincident(g1,g0)
    c: Coincident(g1,g-5)
    c: Coincident(g2,g1)
    c: Coincident(g2,g-5)
    c: Coincident(g3,g2)
    c: Coincident(g3,g0)
FEATURE [PartDesign::Pad] Pad012
  BaseFeature = -> Pad011
  Direction = (-1.9e-15,-1,1e-16)
  Length = 1.5
  Length2 = 10
  Placement = pos=(0,0,0) rot=(1,1,1;2.0944rad)
  Profile = -> Sketch021
  ReferenceAxis = -> Sketch021 [N_Axis]
  Refine = true
  Reversed = true
  Suppressed = false
  Type = 0
FEATURE [Sketcher::SketchObject] Sketch022
  ArcFitTolerance = 1e-06
  AttachmentSupport = -> [Pad012]
  ExternalGeometry = -> [Pad012]
  FullyConstrained = true
  MakeInternals = false
  MapMode = 5
  Placement = pos=(4e-15,4.25e-14,9) rot=(0,0,-1;1.5708rad)
  sketch-geometry (4):
    g0: LineSegment StartX=21.8 StartY=3.2 StartZ=0 EndX=21.8 EndY=8.8 EndZ=0
    g1: LineSegment StartX=21.8 StartY=8.8 StartZ=0 EndX=25.8 EndY=8.8 EndZ=0
    g2: LineSegment StartX=21.8 StartY=3.2 StartZ=0 EndX=25.8 EndY=3.2 EndZ=0
    g3: ArcOfCircle CenterX=25.8 CenterY=6 CenterZ=0 NormalX=0 NormalY=0 NormalZ=1 AngleXU=0 Radius=2.8 StartAngle=4.71239 EndAngle=7.85398
  constraints (13):
    c: PointOnObject(g0,g-3)
    c: Vertical(g0)
    c: Coincident(g1,g0)
    c: Horizontal(g1)
    c: Horizontal(g2)
    c: Coincident(g3,g1)
    c: Coincident(g3,g2)
    c: DistanceY(g0,g0) = 5.6
    c: Coincident(g2,g0)
    c: DistanceY(g-4,g0) = 0.2
    c: DistanceX(g3,g1) = 0
    c: DistanceX(g3,g2) = 0
    c: DistanceX(g1,g1) = 4
FEATURE [PartDesign::Pad] Pad013
  BaseFeature = -> Pad012
  Direction = (0,5.3e-15,1)
  Length = 5
  Length2 = 10
  Placement = pos=(0,0,0) rot=(1,1,1;2.0944rad)
  Profile = -> Sketch022
  ReferenceAxis = -> Sketch022 [N_Axis]
  Refine = true
  Suppressed = false
  Type = 0
FEATURE [PartDesign::Pad] Pad014
  BaseFeature = -> Pad013
  Direction = (0,5.3e-15,1)
  Length = 8
  Length2 = 10
  Placement = pos=(0,0,0) rot=(1,1,1;2.0944rad)
  Profile = -> Sketch022
  ReferenceAxis = -> Sketch022 [N_Axis]
  Refine = true
  Reversed = true
  Suppressed = false
  Type = 0
FEATURE [Sketcher::SketchObject] Sketch023
  ArcFitTolerance = 1e-06
  AttachmentSupport = -> [Pad014]
  ExternalGeometry = -> [Pad014]
  FullyConstrained = true
  MakeInternals = false
  MapMode = 5
  Placement = pos=(17.5,0,1.4e-14) rot=(0.57735,0.57735,-0.57735;4.18879rad)
  sketch-geometry (5):
    g0: LineSegment StartX=-26.9 StartY=-1 StartZ=0 EndX=-20.3 EndY=-1 EndZ=0
    g1: LineSegment StartX=-20.3 StartY=-1 StartZ=0 EndX=-20.3 EndY=-7.5 EndZ=0
    g2: LineSegment StartX=-20.3 StartY=-7.5 StartZ=0 EndX=-24.2928 EndY=-7.5 EndZ=0
    g3: LineSegment StartX=-24.2928 StartY=-7.5 StartZ=0 EndX=-26.9 EndY=-3.54962 EndZ=0
    g4: LineSegment StartX=-26.9 StartY=-3.54962 StartZ=0 EndX=-26.9 EndY=-1 EndZ=0
  constraints (11):
    c: Coincident(g0,g-7)
    c: Coincident(g0,g-4)
    c: Coincident(g1,g0)
    c: PointOnObject(g1,g-4)
    c: Coincident(g2,g1)
    c: Coincident(g2,g-6)
    c: Horizontal(g2)
    c: Coincident(g3,g2)
    c: Coincident(g3,g-7)
    c: Coincident(g4,g3)
    c: Coincident(g4,g0)
FEATURE [PartDesign::Pocket] Pocket008
  BaseFeature = -> Pad014
  Direction = (1,0,1.3e-15)
  Length = 13
  Length2 = 5
  Placement = pos=(0,0,0) rot=(1,1,1;2.0944rad)
  Profile = -> Sketch023
  ReferenceAxis = -> Sketch023 [N_Axis]
  Refine = true
  Reversed = true
  Suppressed = false
  Type = 0
FEATURE [PartDesign::Body] Body  label="Rear_Torso"
  AllowCompound = false
  Group = -> [Sketch,Pad,Sketch001,Pad001,Sketch002,Pad002,Sketch003,Pad003,Sketch004,Pocket,Sketch005,Sketch006,Pocket002,Pocket003,Sketch007,Pad004,Sketch008,Pad005,Sketch009,Pocket004,Sketch010,Pad006,Sketch011,Pocket005,Sketch012,Pocket006,Sketch015,Pad007,Sketch016,Pocket007,Sketch017,Pad008,Sketch018,Pad009,Sketch019,Pad010,Sketch020,Pad011,Sketch021,Pad012,Sketch022,Pad013,Pad014,Sketch023,Pocket008,+36 more]
  Origin = -> Origin
  Placement = pos=(33,19,0) rot=(0,0,1;0rad)
  Tip = -> Pocket017
COMPONENT P1 — recipe-attached ("Lower_Mix_Drum", modeled in this document).
Construction recipe (the document's own serialized feature program — sketch geometry with constraints, then the solid features built on it; lengths are millimeters unless a unit is written):

FEATURE [Sketcher::SketchObject] Sketch013
  ArcFitTolerance = 1e-06
  AttachmentSupport = -> [XY_Plane001]
  FullyConstrained = true
  MakeInternals = false
  MapMode = 5
  sketch-geometry (27):
    g0: LineSegment StartX=10.95 StartY=0 StartZ=0 EndX=10.2116 EndY=11.7914 EndZ=0
    g1: LineSegment StartX=10.1227 StartY=12.1452 StartZ=0 EndX=8.45642 EndY=15.7837 EndZ=0
    g2: LineSegment StartX=8.05744 StartY=16.2274 StartZ=0 EndX=5.30529 EndY=17.86 EndZ=0
    g3: ArcOfCircle CenterX=9.21355 CenterY=11.7289 CenterZ=0 NormalX=0 NormalY=0 NormalZ=1 AngleXU=0 Radius=1 StartAngle=0.0625408 EndAngle=0.429466
    g4: GeomPoint [constr] X=10.2 Y=11.9765 Z=0
    g5: ArcOfCircle CenterX=7.54723 CenterY=15.3673 CenterZ=0 NormalX=0 NormalY=0 NormalZ=1 AngleXU=0 Radius=1 StartAngle=0.429466 EndAngle=1.03536
    g6: GeomPoint [constr] X=8.32627 Y=16.0679 Z=0
    g7: ArcOfCircle CenterX=4.79507 CenterY=17 CenterZ=0 NormalX=0 NormalY=0 NormalZ=1 AngleXU=0 Radius=1 StartAngle=1.03536 EndAngle=1.5708
    g8: LineSegment StartX=10.95 StartY=0 StartZ=0 EndX=9.95 EndY=0 EndZ=0
    g9: LineSegment StartX=9.95 StartY=0 StartZ=0 EndX=9.95 EndY=1 EndZ=0
    g10: LineSegment StartX=9.95 StartY=1 StartZ=0 EndX=9.45 EndY=1 EndZ=0
    g11: LineSegment StartX=9.45 StartY=1 StartZ=0 EndX=8.80722 EndY=11.2644 EndZ=0
    g12: LineSegment StartX=8.71836 StartY=11.6182 StartZ=0 EndX=7.14 EndY=15.0646 EndZ=0
    g13: LineSegment StartX=6.74102 StartY=15.5083 StartZ=0 EndX=5.30528 EndY=16.36 EndZ=0
    g14: LineSegment StartX=4.79506 StartY=16.5 StartZ=0 EndX=0 EndY=16.5 EndZ=0
    g15: ArcOfCircle CenterX=4.79506 CenterY=15.5 CenterZ=0 NormalX=0 NormalY=0 NormalZ=1 AngleXU=0 Radius=1 StartAngle=1.03536 EndAngle=1.5708
    g16: GeomPoint [constr] X=5.06937 Y=16.5 Z=0
    g17: ArcOfCircle CenterX=6.23081 CenterY=14.6483 CenterZ=0 NormalX=0 NormalY=0 NormalZ=1 AngleXU=0 Radius=1 StartAngle=0.429466 EndAngle=1.03536
    g18: GeomPoint [constr] X=7.00985 Y=15.3488 Z=0
    g19: ArcOfCircle CenterX=7.80918 CenterY=11.2019 CenterZ=0 NormalX=0 NormalY=0 NormalZ=1 AngleXU=0 Radius=1 StartAngle=0.0625408 EndAngle=0.429466
    g20: GeomPoint [constr] X=8.79562 Y=11.4495 Z=0
    g21: LineSegment StartX=4.79507 StartY=18 StartZ=0 EndX=2.15 EndY=18 EndZ=0
    g22: ArcOfCircle CenterX=2.15 CenterY=19 CenterZ=0 NormalX=0 NormalY=0 NormalZ=1 AngleXU=0 Radius=1 StartAngle=3.14159 EndAngle=4.71239
    g23: LineSegment StartX=1.15 StartY=19 StartZ=0 EndX=1.15 EndY=20.9 EndZ=0
    g24: ArcOfCircle CenterX=0.65 CenterY=20.9 CenterZ=0 NormalX=0 NormalY=0 NormalZ=1 AngleXU=0 Radius=0.5 StartAngle=3e-16 EndAngle=1.5708
    g25: LineSegment StartX=0.65 StartY=21.4 StartZ=0 EndX=0 EndY=21.4 EndZ=0
    g26: LineSegment StartX=0 StartY=21.4 StartZ=0 EndX=0 EndY=16.5 EndZ=0
  constraints (72):
    c: PointOnObject(g0,g-1)
    c: DistanceX(g-1,g0) = 10.95
    c: DistanceX(g-1,g4) = 10.2
    c: Distance(g4,g0) = 12
    c: Distance(g6,g4) = 4.5
    c: PointOnObject(g4,g0)
    c: PointOnObject(g4,g1)
    c: Tangent(g0,g3) = -1.5708
    c: Tangent(g1,g3) = -1.5708
    c: PointOnObject(g6,g1)
    c: PointOnObject(g6,g2)
    c: Tangent(g1,g5) = -1.5708
    c: Tangent(g2,g5) = -1.5708
    c: Tangent(g2,g7) = -1.5708
    c: Radius(g3) = 1
    c: Radius(g5) = 1
    c: Radius(g7) = 1
    c: Coincident(g8,g0)
    c: PointOnObject(g8,g-1)
    c: DistanceX(g8,g8) = 1
    c: Coincident(g9,g8)
    c: Coincident(g10,g9)
    c: Horizontal(g10)
    c: DistanceX(g10,g10) = 0.5
    c: Distance(g9) = 1
    c: Vertical(g9)
    c: Coincident(g11,g10)
    c: PointOnObject(g14,g-2)
    c: Horizontal(g14)
    c: PointOnObject(g16,g13)
    c: PointOnObject(g16,g14)
    c: Tangent(g13,g15) = -1.5708
    c: Tangent(g14,g15) = -1.5708
    c: PointOnObject(g18,g12)
    c: PointOnObject(g18,g13)
    c: Tangent(g12,g17) = -1.5708
    c: Tangent(g13,g17) = -1.5708
    c: PointOnObject(g20,g11)
    c: PointOnObject(g20,g12)
    c: Tangent(g11,g19) = -1.5708
    c: Tangent(g12,g19) = -1.5708
    c: Radius(g15) = 1
    c: Radius(g17) = 1
    c: Radius(g19) = 1
    c: Parallel(g12,g1)
    c: Parallel(g11,g0)
    c: Parallel(g13,g2)
    c: Distance(g11,g0) = 1.5
    c: Distance(g2,g13) = 1.5
    c: Tangent(g21,g7) = -1.5708
    c: Horizontal(g21)
    c: Coincident(g22,g21)
    c: Coincident(g23,g22)
    c: Vertical(g23)
    c: Coincident(g24,g23)
    c: Coincident(g25,g24)
    c: PointOnObject(g25,g-2)
    c: Horizontal(g25)
    c: Coincident(g26,g25)
    c: Coincident(g26,g14)
    c: DistanceX(g25,g22) = 1.15
    c: DistanceY(g21,g25) = 3.4
    c: DistanceY(g14,g21) = 1.5
    c: DistanceY(g23,g24) = 0
    c: DistanceX(g24,g24) = 0
    c: Radius(g24) = 0.5
    c: DistanceY(g22,g22) = 0
    c: DistanceX(g21,g22) = 0
    c: DistanceY(g-1,g21) = 18
    c: Radius(g22) = 1
    c: Distance(g2,g2) = 3.2
    c: Distance(g2,g13) = 1.5
FEATURE [PartDesign::Revolution] Revolution
  Angle = 360
  Angle2 = 60
  Axis = (0,1,0)
  Base = (0,0,0)
  Profile = -> Sketch013
  ReferenceAxis = -> Sketch013 [V_Axis]
  Refine = true
  Reversed = true
  Suppressed = false
  Type = 0
FEATURE [PartDesign::Body] Body001  label="Lower_Mix_Drum"
  AllowCompound = false
  Group = -> [Sketch013,Revolution]
  Origin = -> Origin001
  Placement = pos=(44,14.5663,15.5588) rot=(1,0,0;0.296706rad)
  Tip = -> Revolution
COMPONENT P2 — recipe-attached ("Upper_Mix_Drum", modeled in this document).
Construction recipe (the document's own serialized feature program — sketch geometry with constraints, then the solid features built on it; lengths are millimeters unless a unit is written):

FEATURE [Sketcher::SketchObject] Sketch014
  ArcFitTolerance = 1e-06
  AttachmentSupport = -> [YZ_Plane003]
  FullyConstrained = true
  MakeInternals = false
  MapMode = 5
  Placement = pos=(0,0,0) rot=(0.57735,0.57735,0.57735;2.0944rad)
  sketch-geometry (18):
    g0: LineSegment StartX=0 StartY=10.95 StartZ=0 EndX=-12.0529 EndY=5.63156 EndZ=0
    g1: LineSegment StartX=-12.351 StartY=5.17412 StartZ=0 EndX=-12.351 EndY=4.5 EndZ=0
    g2: LineSegment StartX=-12.351 StartY=4.5 StartZ=0 EndX=-12.731 EndY=4.5 EndZ=0
    g3: LineSegment StartX=-13.031 StartY=4.2 StartZ=0 EndX=-13.031 EndY=1.1 EndZ=0
    g4: LineSegment StartX=0 StartY=10.95 StartZ=0 EndX=0 EndY=9.95 EndZ=0
    g5: LineSegment StartX=0 StartY=9.95 StartZ=0 EndX=1 EndY=9.95 EndZ=0
    g6: LineSegment StartX=1 StartY=9.95 StartZ=0 EndX=1 EndY=9.45 EndZ=0
    g7: LineSegment StartX=1 StartY=9.45 StartZ=0 EndX=0 EndY=9.45 EndZ=0
    g8: LineSegment StartX=0 StartY=9.45 StartZ=0 EndX=-11.531 EndY=4.36183 EndZ=0
    g9: LineSegment StartX=-11.531 StartY=4.36183 StartZ=0 EndX=-11.531 EndY=0 EndZ=0
    g10: LineSegment StartX=-13.031 StartY=1.1 StartZ=0 EndX=-16.031 EndY=1.1 EndZ=0
    g11: ArcOfCircle CenterX=-16.031 CenterY=0.6 CenterZ=0 NormalX=0 NormalY=0 NormalZ=1 AngleXU=0 Radius=0.5 StartAngle=1.5708 EndAngle=3.14159
    g12: LineSegment StartX=-16.531 StartY=0.6 StartZ=0 EndX=-16.531 EndY=0 EndZ=0
    g13: LineSegment StartX=-16.531 StartY=0 StartZ=0 EndX=-11.531 EndY=0 EndZ=0
    g14: ArcOfCircle CenterX=-11.851 CenterY=5.17412 CenterZ=0 NormalX=0 NormalY=0 NormalZ=1 AngleXU=0 Radius=0.5 StartAngle=1.98636 EndAngle=3.14159
    g15: GeomPoint [constr] X=-12.351 Y=5.5 Z=0
    g16: ArcOfCircle CenterX=-12.731 CenterY=4.2 CenterZ=0 NormalX=0 NormalY=0 NormalZ=1 AngleXU=0 Radius=0.3 StartAngle=1.5708 EndAngle=3.14159
    g17: GeomPoint [constr] X=-13.031 Y=4.5 Z=0
  constraints (51):
    c: PointOnObject(g0,g-2)
    c: Vertical(g1)
    c: Coincident(g2,g1)
    c: Horizontal(g2)
    c: Vertical(g3)
    c: Coincident(g4,g0)
    c: PointOnObject(g4,g-2)
    c: Coincident(g5,g4)
    c: Horizontal(g5)
    c: Coincident(g6,g5)
    c: Vertical(g6)
    c: Coincident(g7,g6)
    c: Horizontal(g7)
    c: Coincident(g9,g8)
    c: Vertical(g9)
    c: Coincident(g10,g3)
    c: Horizontal(g10)
    c: Coincident(g11,g10)
    c: Coincident(g12,g11)
    c: Vertical(g12)
    c: Coincident(g13,g12)
    c: Coincident(g13,g9)
    c: Horizontal(g13)
    c: DistanceY(g-1,g0) = 10.95
    c: DistanceY(g-1,g4) = 9.95
    c: DistanceY(g-1,g6) = 9.45
    c: DistanceX(g5,g5) = 1
    c: DistanceX(g7,g7) = 1
    c: Coincident(g8,g7)
    c: Distance(g0,g15) = 13.5
    c: PointOnObject(g9,g-1)
    c: DistanceY(g12,g15) = 5.5
    c: Parallel(g0,g8)
    c: DistanceX(g17,g2) = 0.68
    c: DistanceY(g1,g15) = 1
    c: DistanceY(g9,g3) = 1.1
    c: DistanceX(g17,g8) = 1.5
    c: DistanceX(g12,g9) = 5
    c: DistanceX(g11,g10) = 0
    c: DistanceY(g11,g11) = 0
    c: Radius(g11) = 0.5
    c: PointOnObject(g15,g0)
    c: PointOnObject(g15,g1)
    c: Tangent(g0,g14) = -1.5708
    c: Tangent(g1,g14) = -1.5708
    c: PointOnObject(g17,g2)
    c: PointOnObject(g17,g3)
    c: Tangent(g2,g16) = -1.5708
    c: Tangent(g3,g16) = -1.5708
    c: Radius(g16) = 0.3
    c: Radius(g14) = 0.5
FEATURE [PartDesign::Revolution] Revolution001
  Angle = 360
  Angle2 = 60
  Axis = (0,1,0)
  Base = (0,0,0)
  Placement = pos=(0,0,0) rot=(1,1,1;2.0944rad)
  Profile = -> Sketch014
  ReferenceAxis = -> Sketch014 [H_Axis]
  Refine = true
  Suppressed = false
  Type = 0
FEATURE [PartDesign::Body] Body003  label="Upper_Mix_Drum"
  AllowCompound = false
  Group = -> [Sketch014,Revolution001]
  Origin = -> Origin003
  Placement = pos=(44,14.5663,15.5588) rot=(1,0,0;0.296706rad)
  Tip = -> Revolution001
COMPONENT P3 — recipe-attached ("Front Torso", modeled in this document).
Construction recipe (the document's own serialized feature program — sketch geometry with constraints, then the solid features built on it; lengths are millimeters unless a unit is written):

FEATURE [Sketcher::SketchObject] Sketch031
  ArcFitTolerance = 1e-06
  AttachmentSupport = -> [Binder010]
  ExternalGeometry = -> [Binder010]
  FullyConstrained = true
  MakeInternals = false
  MapMode = 5
  Placement = pos=(4.65e-14,0,-5) rot=(1,0,0;3.14159rad)
  sketch-geometry (13):
    g0: LineSegment StartX=0 StartY=21.3 StartZ=0 EndX=1.5 EndY=21.3 EndZ=0
    g1: LineSegment StartX=1.5 StartY=21.3 StartZ=0 EndX=1.5 EndY=14.5 EndZ=0
    g2: LineSegment StartX=1.5 StartY=14.5 StartZ=0 EndX=6 EndY=14.5 EndZ=0
    g3: LineSegment StartX=6 StartY=14.5 StartZ=0 EndX=6 EndY=13 EndZ=0
    g4: LineSegment StartX=6 StartY=13 StartZ=0 EndX=1.5 EndY=8.5 EndZ=0
    g5: LineSegment StartX=0 StartY=21.3 StartZ=0 EndX=0 EndY=13 EndZ=0
    g6: LineSegment StartX=0 StartY=13 StartZ=0 EndX=4 EndY=13 EndZ=0
    g7: LineSegment StartX=4 StartY=13 StartZ=0 EndX=0 EndY=9 EndZ=0
    g8: LineSegment StartX=0 StartY=9 StartZ=0 EndX=0 EndY=2 EndZ=0
    g9: LineSegment StartX=1.5 StartY=8.5 StartZ=0 EndX=1.5 EndY=3.5 EndZ=0
    g10: LineSegment StartX=1.5 StartY=3.5 StartZ=0 EndX=3 EndY=3.5 EndZ=0
    g11: LineSegment StartX=3 StartY=3.5 StartZ=0 EndX=3 EndY=2 EndZ=0
    g12: LineSegment StartX=3 StartY=2 StartZ=0 EndX=0 EndY=2 EndZ=0
  constraints (26):
    c: Coincident(g0,g-5)
    c: Coincident(g0,g-4)
    c: Coincident(g1,g0)
    c: Coincident(g1,g-7)
    c: Coincident(g2,g1)
    c: Coincident(g2,g-8)
    c: Coincident(g3,g2)
    c: Coincident(g3,g-10)
    c: Coincident(g4,g3)
    c: Coincident(g4,g-11)
    c: Coincident(g5,g0)
    c: Coincident(g5,g-6)
    c: Coincident(g6,g5)
    c: Coincident(g6,g-9)
    c: Coincident(g7,g6)
    c: Coincident(g7,g-15)
    c: Coincident(g8,g7)
    c: Coincident(g8,g-15)
    c: Coincident(g9,g4)
    c: Coincident(g9,g-12)
    c: Coincident(g10,g9)
    c: Coincident(g10,g-13)
    c: Coincident(g11,g10)
    c: Coincident(g11,g-14)
    c: Coincident(g12,g11)
    c: Coincident(g12,g8)
FEATURE [PartDesign::Pad] Pad034
  Direction = (9.3e-15,0,-1)
  Length = 4
  Length2 = 10
  Profile = -> Sketch031
  ReferenceAxis = -> Sketch031 [N_Axis]
  Refine = true
  Suppressed = false
  Type = 0
FEATURE [Sketcher::SketchObject] Sketch032
  ArcFitTolerance = 1e-06
  AttachmentSupport = -> [Pad034]
  ExternalGeometry = -> [Pad034]
  FullyConstrained = true
  MakeInternals = false
  MapMode = 5
  Placement = pos=(8.38e-14,0,-9) rot=(1,0,0;3.14159rad)
  sketch-geometry (10):
    g0: LineSegment StartX=4e-16 StartY=21.3 StartZ=0 EndX=22 EndY=21.3 EndZ=0
    g1: LineSegment StartX=22 StartY=21.3 StartZ=0 EndX=22 EndY=13 EndZ=0
    g2: LineSegment StartX=22 StartY=13 StartZ=0 EndX=18 EndY=13 EndZ=0
    g3: LineSegment StartX=18 StartY=13 StartZ=0 EndX=22 EndY=9 EndZ=0
    g4: LineSegment StartX=22 StartY=9 StartZ=0 EndX=22 EndY=-7 EndZ=0
    g5: LineSegment StartX=22 StartY=-7 StartZ=0 EndX=0 EndY=-7 EndZ=0
    g6: LineSegment StartX=0 StartY=-7 StartZ=0 EndX=0 EndY=9 EndZ=0
    g7: LineSegment StartX=0 StartY=9 StartZ=0 EndX=4 EndY=13 EndZ=0
    g8: LineSegment StartX=4 StartY=13 StartZ=0 EndX=0 EndY=13 EndZ=0
    g9: LineSegment StartX=0 StartY=13 StartZ=0 EndX=4e-16 EndY=21.3 EndZ=0
  constraints (26):
    c: Coincident(g0,g-4)
    c: Horizontal(g0)
    c: Coincident(g1,g0)
    c: Vertical(g1)
    c: Coincident(g2,g1)
    c: Horizontal(g2)
    c: Coincident(g3,g2)
    c: Coincident(g4,g3)
    c: Vertical(g4)
    c: Coincident(g5,g4)
    c: PointOnObject(g5,g-2)
    c: Horizontal(g5)
    c: Coincident(g6,g5)
    c: Coincident(g6,g-7)
    c: Coincident(g7,g6)
    c: Coincident(g7,g-6)
    c: Coincident(g8,g7)
    c: Coincident(g8,g-5)
    c: Coincident(g9,g8)
    c: Coincident(g9,g0)
    c: DistanceX(g0,g0) = 22
    c: DistanceY(g1,g1) = 8.3
    c: DistanceX(g5,g5) = 22
    c: DistanceY(g6,g6) = 16
    c: DistanceY(g4,g4) = 16
    c: DistanceX(g2,g2) = 4
FEATURE [PartDesign::Pad] Pad035
  BaseFeature = -> Pad034
  Direction = (9.3e-15,0,-1)
  Length = 3
  Length2 = 10
  Profile = -> Sketch032
  ReferenceAxis = -> Sketch032 [N_Axis]
  Refine = true
  Suppressed = false
  Type = 0
FEATURE [Sketcher::SketchObject] Sketch033
  ArcFitTolerance = 1e-06
  AttachmentSupport = -> [Pad035]
  ExternalGeometry = -> [Pad035]
  FullyConstrained = true
  MakeInternals = false
  MapMode = 5
  Placement = pos=(8.35e-14,0,-9) rot=(0,0,1;0rad)
  sketch-geometry (13):
    g0: LineSegment StartX=22 StartY=-21.3 StartZ=0 EndX=20.5 EndY=-21.3 EndZ=0
    g1: LineSegment StartX=22 StartY=-21.3 StartZ=0 EndX=22 EndY=-13 EndZ=0
    g2: LineSegment StartX=20.5 StartY=-21.3 StartZ=0 EndX=20.5 EndY=-14.5 EndZ=0
    g3: LineSegment StartX=22 StartY=-13 StartZ=0 EndX=18 EndY=-13 EndZ=0
    g4: LineSegment StartX=18 StartY=-13 StartZ=0 EndX=22 EndY=-9 EndZ=0
    g5: LineSegment StartX=22 StartY=-9 StartZ=0 EndX=22 EndY=-2 EndZ=0
    g6: LineSegment StartX=22 StartY=-2 StartZ=0 EndX=19 EndY=-2 EndZ=0
    g7: LineSegment StartX=19 StartY=-2 StartZ=0 EndX=19 EndY=-3.5 EndZ=0
    g8: LineSegment StartX=20.5 StartY=-3.5 StartZ=0 EndX=19 EndY=-3.5 EndZ=0
    g9: LineSegment StartX=20.5 StartY=-3.5 StartZ=0 EndX=20.5 EndY=-8.5 EndZ=0
    g10: LineSegment StartX=20.5 StartY=-8.5 StartZ=0 EndX=16 EndY=-13 EndZ=0
    g11: LineSegment StartX=16 StartY=-13 StartZ=0 EndX=16 EndY=-14.5 EndZ=0
    g12: LineSegment StartX=16 StartY=-14.5 StartZ=0 EndX=20.5 EndY=-14.5 EndZ=0
  constraints (35):
    c: Horizontal(g0)
    c: DistanceX(g0,g0) = 1.5
    c: DistanceY(g7,g6) = 1.5
    c: DistanceX(g6,g5) = 3
    c: PointOnObject(g5,g-3)
    c: DistanceX(g8,g5) = 1.5
    c: DistanceY(g9,g8) = 5
    c: DistanceY(g-4,g5) = 7
    c: DistanceY(g0,g2) = 6.8
    c: DistanceX(g11,g2) = 4.5
    c: DistanceY(g11,g10) = 1.5
    c: Coincident(g1,g0)
    c: Coincident(g2,g0)
    c: Vertical(g2)
    c: Coincident(g3,g1)
    c: Coincident(g4,g3)
    c: Coincident(g5,g4)
    c: Coincident(g6,g5)
    c: Horizontal(g6)
    c: Coincident(g7,g6)
    c: Vertical(g7)
    c: Coincident(g8,g7)
    c: Horizontal(g8)
    c: Coincident(g9,g8)
    c: Vertical(g9)
    c: Coincident(g10,g9)
    c: Coincident(g11,g10)
    c: Vertical(g11)
    c: Coincident(g12,g11)
    c: Coincident(g12,g2)
    c: Horizontal(g12)
    c: Coincident(g4,g-4)
    c: Coincident(g3,g-5)
    c: Coincident(g1,g-6)
    c: Coincident(g0,g-8)
FEATURE [PartDesign::Pad] Pad036
  BaseFeature = -> Pad035
  Direction = (-9.3e-15,0,1)
  Length = 4
  Length2 = 10
  Profile = -> Sketch033
  ReferenceAxis = -> Sketch033 [N_Axis]
  Refine = true
  Suppressed = false
  Type = 0
FEATURE [Sketcher::SketchObject] Sketch034
  ArcFitTolerance = 1e-06
  AttachmentSupport = -> [Pad036]
  ExternalGeometry = -> [Pad036]
  FullyConstrained = true
  MakeInternals = false
  MapMode = 5
  Placement = pos=(8.35e-14,0,-9) rot=(0,0,1;0rad)
  sketch-geometry (8):
    g0: LineSegment StartX=0 StartY=7 StartZ=0 EndX=0 EndY=5 EndZ=0
    g1: LineSegment StartX=0 StartY=5 StartZ=0 EndX=22 EndY=5 EndZ=0
    g2: LineSegment StartX=22 StartY=5 StartZ=0 EndX=22 EndY=7 EndZ=0
    g3: LineSegment StartX=22 StartY=7 StartZ=0 EndX=0 EndY=7 EndZ=0
    g4: LineSegment StartX=3 StartY=-2 StartZ=0 EndX=3 EndY=-3.5 EndZ=0
    g5: LineSegment StartX=3 StartY=-3.5 StartZ=0 EndX=19 EndY=-3.5 EndZ=0
    g6: LineSegment StartX=19 StartY=-3.5 StartZ=0 EndX=19 EndY=-2 EndZ=0
    g7: LineSegment StartX=19 StartY=-2 StartZ=0 EndX=3 EndY=-2 EndZ=0
  constraints (21):
    c: Coincident(g0,g1)
    c: Coincident(g1,g2)
    c: Coincident(g2,g3)
    c: Coincident(g3,g0)
    c: Vertical(g0)
    c: Vertical(g2)
    c: Horizontal(g1)
    c: Horizontal(g3)
    c: Coincident(g0,g-3)
    c: PointOnObject(g1,g-4)
    c: Coincident(g4,g5)
    c: Coincident(g5,g6)
    c: Coincident(g6,g7)
    c: Coincident(g7,g4)
    c: Vertical(g4)
    c: Vertical(g6)
    c: Horizontal(g5)
    c: Horizontal(g7)
    c: Coincident(g4,g-6)
    c: Coincident(g5,g-5)
    c: DistanceY(g2,g2) = 2
FEATURE [PartDesign::Pad] Pad037
  BaseFeature = -> Pad036
  Direction = (-9.3e-15,0,1)
  Length = 2
  Length2 = 10
  Profile = -> Sketch034 [Edge7,Edge8,Edge6,Edge5]
  ReferenceAxis = -> Sketch034 [N_Axis]
  Refine = true
  Suppressed = false
  Type = 0
FEATURE [PartDesign::Pad] Pad038
  BaseFeature = -> Pad037
  Direction = (-9.3e-15,0,1)
  Length = 4
  Length2 = 10
  Profile = -> Sketch034 [Edge4,Edge1,Edge2,Edge3]
  ReferenceAxis = -> Sketch034 [N_Axis]
  Refine = true
  Suppressed = false
  Type = 0
FEATURE [Sketcher::SketchObject] Sketch036
  ArcFitTolerance = 1e-06
  AttachmentSupport = -> [Pad038]
  ExternalGeometry = -> [Pad038]
  FullyConstrained = true
  MakeInternals = false
  MapMode = 5
  Placement = pos=(8.35e-14,0,-9) rot=(0,0,1;0rad)
  sketch-geometry (6):
    g0: LineSegment StartX=16 StartY=-14.5 StartZ=0 EndX=16 EndY=-15 EndZ=0
    g1: LineSegment StartX=16 StartY=-15 StartZ=0 EndX=20 EndY=-15 EndZ=0
    g2: LineSegment StartX=20 StartY=-15 StartZ=0 EndX=20 EndY=-21.3 EndZ=0
    g3: LineSegment StartX=20 StartY=-21.3 StartZ=0 EndX=20.5 EndY=-21.3 EndZ=0
    g4: LineSegment StartX=20.5 StartY=-21.3 StartZ=0 EndX=20.5 EndY=-14.5 EndZ=0
    g5: LineSegment StartX=20.5 StartY=-14.5 StartZ=0 EndX=16 EndY=-14.5 EndZ=0
  constraints (15):
    c: Coincident(g0,g-7)
    c: Vertical(g0)
    c: Coincident(g1,g0)
    c: Horizontal(g1)
    c: Coincident(g2,g1)
    c: PointOnObject(g2,g-5)
    c: Vertical(g2)
    c: Coincident(g3,g2)
    c: Coincident(g3,g-6)
    c: Coincident(g4,g3)
    c: Coincident(g4,g-7)
    c: Coincident(g5,g4)
    c: Coincident(g5,g0)
    c: DistanceX(g2,g3) = 0.5
    c: DistanceY(g0,g0) = 0.5
FEATURE [PartDesign::Pad] Pad042
  BaseFeature = -> Pad038
  Direction = (-9.3e-15,0,1)
  Length = 4
  Length2 = 10
  Profile = -> Sketch036
  ReferenceAxis = -> Sketch036 [N_Axis]
  Refine = true
  Suppressed = false
  Type = 0
FEATURE [Sketcher::SketchObject] Sketch037
  ArcFitTolerance = 1e-06
  AttachmentSupport = -> [Pad042]
  ExternalGeometry = -> [Pad042]
  FullyConstrained = true
  MakeInternals = false
  MapMode = 5
  Placement = pos=(8.35e-14,0,-9) rot=(0,0,1;0rad)
  sketch-geometry (6):
    g0: LineSegment StartX=6 StartY=-14.5 StartZ=0 EndX=6 EndY=-15 EndZ=0
    g1: LineSegment StartX=6 StartY=-15 StartZ=0 EndX=2 EndY=-15 EndZ=0
    g2: LineSegment StartX=2 StartY=-15 StartZ=0 EndX=2 EndY=-21.3 EndZ=0
    g3: LineSegment StartX=2 StartY=-21.3 StartZ=0 EndX=1.5 EndY=-21.3 EndZ=0
    g4: LineSegment StartX=1.5 StartY=-21.3 StartZ=0 EndX=1.5 EndY=-14.5 EndZ=0
    g5: LineSegment StartX=1.5 StartY=-14.5 StartZ=0 EndX=6 EndY=-14.5 EndZ=0
  constraints (15):
    c: Coincident(g0,g-3)
    c: Vertical(g0)
    c: Coincident(g1,g0)
    c: Horizontal(g1)
    c: Coincident(g2,g1)
    c: PointOnObject(g2,g-5)
    c: Vertical(g2)
    c: Coincident(g3,g2)
    c: Coincident(g3,g-5)
    c: Coincident(g4,g3)
    c: Coincident(g4,g-4)
    c: Coincident(g5,g4)
    c: Coincident(g5,g0)
    c: DistanceX(g3,g2) = 0.5
    c: DistanceY(g0,g0) = 0.5
FEATURE [PartDesign::Pad] Pad043
  BaseFeature = -> Pad042
  Direction = (-9.3e-15,0,1)
  Length = 4
  Length2 = 10
  Profile = -> Sketch037
  ReferenceAxis = -> Sketch037 [N_Axis]
  Refine = true
  Suppressed = false
  Type = 0
FEATURE [Sketcher::SketchObject] Sketch038
  ArcFitTolerance = 1e-06
  AttachmentSupport = -> [Pad043]
  ExternalGeometry = -> [Pad043]
  FullyConstrained = true
  MakeInternals = false
  MapMode = 5
  Placement = pos=(8.35e-14,0,-9) rot=(0,0,1;0rad)
  sketch-geometry (6):
    g0: LineSegment StartX=19 StartY=-3.5 StartZ=0 EndX=19 EndY=-4 EndZ=0
    g1: LineSegment StartX=19 StartY=-4 StartZ=0 EndX=20 EndY=-4 EndZ=0
    g2: LineSegment StartX=20 StartY=-4 StartZ=0 EndX=20 EndY=-9 EndZ=0
    g3: LineSegment StartX=19 StartY=-3.5 StartZ=0 EndX=20.5 EndY=-3.5 EndZ=0
    g4: LineSegment StartX=20.5 StartY=-3.5 StartZ=0 EndX=20.5 EndY=-8.5 EndZ=0
    g5: LineSegment StartX=20.5 StartY=-8.5 StartZ=0 EndX=20 EndY=-9 EndZ=0
  constraints (15):
    c: Coincident(g0,g-3)
    c: Coincident(g1,g0)
    c: Horizontal(g1)
    c: Coincident(g2,g1)
    c: PointOnObject(g2,g-5)
    c: Vertical(g2)
    c: Vertical(g0)
    c: DistanceX(g1,g-4) = 0.5
    c: DistanceY(g0,g0) = 0.5
    c: Coincident(g3,g0)
    c: Coincident(g3,g-4)
    c: Coincident(g4,g3)
    c: Coincident(g4,g-5)
    c: Coincident(g5,g4)
    c: Coincident(g5,g2)
FEATURE [PartDesign::Pad] Pad044
  BaseFeature = -> Pad043
  Direction = (-9.3e-15,0,1)
  Length = 4
  Length2 = 10
  Profile = -> Sketch038
  ReferenceAxis = -> Sketch038 [N_Axis]
  Refine = true
  Suppressed = false
  Type = 0
FEATURE [Sketcher::SketchObject] Sketch039
  ArcFitTolerance = 1e-06
  AttachmentSupport = -> [Pad044]
  ExternalGeometry = -> [Pad044]
  FullyConstrained = true
  MakeInternals = false
  MapMode = 5
  Placement = pos=(8.35e-14,0,-9) rot=(0,0,1;0rad)
  sketch-geometry (6):
    g0: LineSegment StartX=3 StartY=-3.5 StartZ=0 EndX=3 EndY=-4 EndZ=0
    g1: LineSegment StartX=3 StartY=-4 StartZ=0 EndX=2 EndY=-4 EndZ=0
    g2: LineSegment StartX=2 StartY=-4 StartZ=0 EndX=2 EndY=-9 EndZ=0
    g3: LineSegment StartX=3 StartY=-3.5 StartZ=0 EndX=1.5 EndY=-3.5 EndZ=0
    g4: LineSegment StartX=1.5 StartY=-3.5 StartZ=0 EndX=1.5 EndY=-8.5 EndZ=0
    g5: LineSegment StartX=1.5 StartY=-8.5 StartZ=0 EndX=2 EndY=-9 EndZ=0
  constraints (15):
    c: Coincident(g0,g-3)
    c: Vertical(g0)
    c: Coincident(g1,g0)
    c: Horizontal(g1)
    c: Coincident(g2,g1)
    c: PointOnObject(g2,g-5)
    c: Vertical(g2)
    c: Coincident(g3,g0)
    c: Coincident(g3,g-4)
    c: Coincident(g4,g3)
    c: Coincident(g4,g-5)
    c: Coincident(g5,g4)
    c: Coincident(g5,g2)
    c: DistanceY(g0,g0) = 0.5
    c: DistanceX(g3,g1) = 0.5
FEATURE [PartDesign::Pad] Pad045
  BaseFeature = -> Pad044
  Direction = (-9.3e-15,0,1)
  Length = 4
  Length2 = 10
  Profile = -> Sketch039
  ReferenceAxis = -> Sketch039 [N_Axis]
  Refine = true
  Suppressed = false
  Type = 0
FEATURE [Sketcher::SketchObject] Sketch040
  ArcFitTolerance = 1e-06
  AttachmentSupport = -> [Pad045]
  ExternalGeometry = -> [Pad045]
  FullyConstrained = true
  MakeInternals = false
  MapMode = 5
  Placement = pos=(8.35e-14,0,-9) rot=(0,0,1;0rad)
  sketch-geometry (4):
    g0: LineSegment StartX=19 StartY=-3.5 StartZ=0 EndX=3 EndY=-3.5 EndZ=0
    g1: LineSegment StartX=3 StartY=-3.5 StartZ=0 EndX=3 EndY=-4 EndZ=0
    g2: LineSegment StartX=3 StartY=-4 StartZ=0 EndX=19 EndY=-4 EndZ=0
    g3: LineSegment StartX=19 StartY=-4 StartZ=0 EndX=19 EndY=-3.5 EndZ=0
  constraints (10):
    c: Coincident(g0,g1)
    c: Coincident(g1,g2)
    c: Coincident(g2,g3)
    c: Coincident(g3,g0)
    c: Horizontal(g0)
    c: Horizontal(g2)
    c: Vertical(g1)
    c: Vertical(g3)
    c: Coincident(g0,g-4)
    c: Coincident(g1,g-3)
FEATURE [PartDesign::Pad] Pad046
  BaseFeature = -> Pad045
  Direction = (-9.3e-15,0,1)
  Length = 2
  Length2 = 10
  Profile = -> Sketch040
  ReferenceAxis = -> Sketch040 [N_Axis]
  Refine = true
  Suppressed = false
  Type = 0
FEATURE [Sketcher::SketchObject] Sketch041
  ArcFitTolerance = 1e-06
  AttachmentSupport = -> [Pad046]
  FullyConstrained = true
  MakeInternals = false
  MapMode = 5
  Placement = pos=(8.35e-14,0,-9) rot=(0,0,1;0rad)
  sketch-geometry (2):
    g0: Circle CenterX=18 CenterY=-7.5 CenterZ=0 NormalX=0 NormalY=0 NormalZ=1 AngleXU=0 Radius=1
    g1: Circle CenterX=4 CenterY=-7.5 CenterZ=0 NormalX=0 NormalY=0 NormalZ=1 AngleXU=0 Radius=1
  constraints (6):
    c: Diameter(g1) = 2
    c: Diameter(g0) = 2
    c: DistanceX(g-1,g1) = 4
    c: DistanceX(g-1,g0) = 18
    c: DistanceY(g1,g-1) = 7.5
    c: DistanceY(g0,g-1) = 7.5
FEATURE [PartDesign::Pocket] Pocket178
  BaseFeature = -> Pad046
  Direction = (9.3e-15,0,-1)
  Length = 5
  Length2 = 5
  Profile = -> Sketch041
  ReferenceAxis = -> Sketch041 [N_Axis]
  Refine = true
  Suppressed = false
  Type = 0
FEATURE [Sketcher::SketchObject] Sketch042
  ArcFitTolerance = 1e-06
  AttachmentSupport = -> [Pocket178]
  ExternalGeometry = -> [Pocket178]
  FullyConstrained = true
  MakeInternals = false
  MapMode = 5
  Placement = pos=(8.35e-14,0,-9) rot=(0,0,1;0rad)
  sketch-geometry (4):
    g0: Circle CenterX=4 CenterY=-7.5 CenterZ=0 NormalX=0 NormalY=0 NormalZ=1 AngleXU=0 Radius=2.1
    g1: Circle CenterX=4 CenterY=-7.5 CenterZ=0 NormalX=0 NormalY=0 NormalZ=1 AngleXU=0 Radius=3.25
    g2: Circle CenterX=18 CenterY=-7.5 CenterZ=0 NormalX=0 NormalY=0 NormalZ=1 AngleXU=0 Radius=2.1
    g3: Circle CenterX=18 CenterY=-7.5 CenterZ=0 NormalX=0 NormalY=0 NormalZ=1 AngleXU=0 Radius=3.25
  constraints (8):
    c: Coincident(g0,g-3)
    c: Coincident(g1,g0)
    c: Coincident(g2,g-4)
    c: Coincident(g3,g2)
    c: Diameter(g0) = 4.2
    c: Diameter(g2) = 4.2
    c: Diameter(g1) = 6.5
    c: Diameter(g3) = 6.5
FEATURE [Sketcher::SketchObject] Sketch043
  ArcFitTolerance = 1e-06
  AttachmentSupport = -> [Pocket178]
  ExternalGeometry = -> [Pocket178]
  FullyConstrained = true
  MakeInternals = false
  MapMode = 5
  Placement = pos=(0,-4,0) rot=(1,0,0;1.5708rad)
  sketch-geometry (8):
    g0: LineSegment StartX=20 StartY=-5 StartZ=0 EndX=19 EndY=-5 EndZ=0
    g1: LineSegment StartX=19 StartY=-5 StartZ=0 EndX=19 EndY=-9 EndZ=0
    g2: LineSegment StartX=19 StartY=-9 StartZ=0 EndX=20 EndY=-9 EndZ=0
    g3: LineSegment StartX=20 StartY=-9 StartZ=0 EndX=20 EndY=-5 EndZ=0
    g4: LineSegment StartX=3 StartY=-5 StartZ=0 EndX=2 EndY=-5 EndZ=0
    g5: LineSegment StartX=2 StartY=-5 StartZ=0 EndX=2 EndY=-9 EndZ=0
    g6: LineSegment StartX=2 StartY=-9 StartZ=0 EndX=3 EndY=-9 EndZ=0
    g7: LineSegment StartX=3 StartY=-9 StartZ=0 EndX=3 EndY=-5 EndZ=0
  constraints (19):
    c: Coincident(g0,g1)
    c: Coincident(g1,g2)
    c: Coincident(g2,g3)
    c: Coincident(g3,g0)
    c: Horizontal(g2)
    c: Vertical(g1)
    c: Coincident(g-9,g0)
    c: Coincident(g0,g-9)
    c: Coincident(g2,g-7)
    c: Coincident(g4,g5)
    c: Coincident(g5,g6)
    c: Coincident(g6,g7)
    c: Coincident(g7,g4)
    c: Horizontal(g6)
    c: Vertical(g5)
    c: Vertical(g7)
    c: Coincident(g4,g-4)
    c: Coincident(g4,g-5)
    c: PointOnObject(g5,g-6)
FEATURE [PartDesign::Pocket] Pocket179
  BaseFeature = -> Pocket178
  Direction = (0,1,-2e-16)
  Length = 0.5
  Length2 = 5
  Profile = -> Sketch043
  ReferenceAxis = -> Sketch043 [N_Axis]
  Refine = true
  Suppressed = false
  Type = 0
FEATURE [Sketcher::SketchObject] Sketch044
  ArcFitTolerance = 1e-06
  AttachmentSupport = -> [Pocket179]
  ExternalGeometry = -> [Pocket179]
  FullyConstrained = true
  MakeInternals = false
  MapMode = 5
  Placement = pos=(6.53e-14,0,-7) rot=(0,0,1;0rad)
  sketch-geometry (8):
    g0: LineSegment StartX=3 StartY=-2 StartZ=0 EndX=3 EndY=-3.5 EndZ=0
    g1: LineSegment StartX=3 StartY=-3.5 StartZ=0 EndX=4.5 EndY=-3.5 EndZ=0
    g2: LineSegment StartX=4.5 StartY=-3.5 StartZ=0 EndX=4.5 EndY=-2 EndZ=0
    g3: LineSegment StartX=4.5 StartY=-2 StartZ=0 EndX=3 EndY=-2 EndZ=0
    g4: LineSegment StartX=19 StartY=-2 StartZ=0 EndX=17.5 EndY=-2 EndZ=0
    g5: LineSegment StartX=17.5 StartY=-2 StartZ=0 EndX=17.5 EndY=-3.5 EndZ=0
    g6: LineSegment StartX=17.5 StartY=-3.5 StartZ=0 EndX=19 EndY=-3.5 EndZ=0
    g7: LineSegment StartX=19 StartY=-3.5 StartZ=0 EndX=19 EndY=-2 EndZ=0
  constraints (20):
    c: Coincident(g0,g1)
    c: Coincident(g1,g2)
    c: Coincident(g2,g3)
    c: Coincident(g3,g0)
    c: Vertical(g2)
    c: Horizontal(g1)
    c: Horizontal(g3)
    c: Coincident(g0,g-4)
    c: Coincident(g4,g5)
    c: Coincident(g5,g6)
    c: Coincident(g6,g7)
    c: Coincident(g7,g4)
    c: Horizontal(g4)
    c: Horizontal(g6)
    c: Vertical(g5)
    c: Coincident(g4,g-6)
    c: Coincident(g-6,g6)
    c: Coincident(g0,g-4)
    c: DistanceX(g3,g3) = 1.5
    c: DistanceX(g4,g4) = 1.5
FEATURE [PartDesign::Pad] Pad047
  BaseFeature = -> Pocket179
  Direction = (-9.3e-15,0,1)
  Length = 2
  Length2 = 10
  Profile = -> Sketch044
  ReferenceAxis = -> Sketch044 [N_Axis]
  Refine = true
  Suppressed = false
  Type = 0
FEATURE [Sketcher::SketchObject] Sketch045
  ArcFitTolerance = 1e-06
  AttachmentSupport = -> [Pad047]
  ExternalGeometry = -> [Pad047]
  FullyConstrained = true
  MakeInternals = false
  MapMode = 5
  Placement = pos=(6.53e-14,0,-7) rot=(0,0,1;0rad)
  sketch-geometry (8):
    g0: LineSegment StartX=19 StartY=-4 StartZ=0 EndX=19 EndY=-3.5 EndZ=0
    g1: LineSegment StartX=19 StartY=-3.5 StartZ=0 EndX=17.5 EndY=-3.5 EndZ=0
    g2: LineSegment StartX=17.5 StartY=-3.5 StartZ=0 EndX=17.5 EndY=-4 EndZ=0
    g3: LineSegment StartX=17.5 StartY=-4 StartZ=0 EndX=19 EndY=-4 EndZ=0
    g4: LineSegment StartX=3 StartY=-4 StartZ=0 EndX=4.5 EndY=-4 EndZ=0
    g5: LineSegment StartX=4.5 StartY=-4 StartZ=0 EndX=4.5 EndY=-3.5 EndZ=0
    g6: LineSegment StartX=4.5 StartY=-3.5 StartZ=0 EndX=3 EndY=-3.5 EndZ=0
    g7: LineSegment StartX=3 StartY=-3.5 StartZ=0 EndX=3 EndY=-4 EndZ=0
  constraints (20):
    c: Coincident(g0,g1)
    c: Coincident(g1,g2)
    c: Coincident(g2,g3)
    c: Coincident(g3,g0)
    c: Vertical(g0)
    c: Vertical(g2)
    c: Horizontal(g1)
    c: Horizontal(g3)
    c: Coincident(g0,g-7)
    c: Coincident(g1,g-6)
    c: Coincident(g4,g5)
    c: Coincident(g5,g6)
    c: Coincident(g6,g7)
    c: Coincident(g7,g4)
    c: Horizontal(g4)
    c: Horizontal(g6)
    c: Vertical(g5)
    c: Vertical(g7)
    c: Coincident(g4,g-4)
    c: Coincident(g5,g-5)
FEATURE [PartDesign::Pocket] Pocket180
  BaseFeature = -> Pad047
  Direction = (9.3e-15,0,-1)
  Length = 2
  Length2 = 5
  Profile = -> Sketch045
  ReferenceAxis = -> Sketch045 [N_Axis]
  Refine = true
  Suppressed = false
  Type = 0
FEATURE [PartDesign::Pad] Pad048
  BaseFeature = -> Pocket180
  Direction = (-9.3e-15,0,1)
  Length = 4
  Length2 = 10
  Profile = -> Sketch042
  ReferenceAxis = -> Sketch042 [N_Axis]
  Refine = true
  Suppressed = false
  Type = 0
FEATURE [PartDesign::Pocket] Pocket181
  BaseFeature = -> Pad048
  Direction = (9.3e-15,0,-1)
  Length = 5
  Length2 = 5
  Profile = -> Sketch042 [Edge1,Edge3]
  ReferenceAxis = -> Sketch042 [N_Axis]
  Refine = true
  Reversed = true
  Suppressed = false
  Type = 0
FEATURE [Sketcher::SketchObject] Sketch046
  ArcFitTolerance = 1e-06
  AttachmentSupport = -> [Pocket181]
  ExternalGeometry = -> [Pocket181]
  FullyConstrained = true
  MakeInternals = false
  MapMode = 5
  Placement = pos=(4.64e-14,0,-5) rot=(0,0,1;0rad)
  sketch-geometry (4):
    g0: LineSegment StartX=8.9 StartY=7 StartZ=0 EndX=8.9 EndY=5 EndZ=0
    g1: LineSegment StartX=8.9 StartY=5 StartZ=0 EndX=13.1 EndY=5 EndZ=0
    g2: LineSegment StartX=13.1 StartY=5 StartZ=0 EndX=13.1 EndY=7 EndZ=0
    g3: LineSegment StartX=13.1 StartY=7 StartZ=0 EndX=8.9 EndY=7 EndZ=0
  constraints (12):
    c: Coincident(g0,g1)
    c: Coincident(g1,g2)
    c: Coincident(g2,g3)
    c: Coincident(g3,g0)
    c: Vertical(g0)
    c: Vertical(g2)
    c: Horizontal(g1)
    c: Horizontal(g3)
    c: PointOnObject(g0,g-3)
    c: PointOnObject(g1,g-4)
    c: DistanceX(g-5,g0) = 8.9
    c: DistanceX(g2,g-6) = 8.9
FEATURE [PartDesign::Pad] Pad049
  BaseFeature = -> Pocket181
  Direction = (-9.3e-15,0,1)
  Length = 2
  Length2 = 10
  Profile = -> Sketch046
  ReferenceAxis = -> Sketch046 [N_Axis]
  Refine = true
  Suppressed = false
  Type = 0
FEATURE [Sketcher::SketchObject] Sketch047
  ArcFitTolerance = 1e-06
  AttachmentSupport = -> [Pad049]
  ExternalGeometry = -> [Pad049]
  FullyConstrained = true
  MakeInternals = false
  MapMode = 5
  Placement = pos=(8.47e-14,4.4e-15,-9) rot=(0,0,1;0rad)
  sketch-geometry (8):
    g0: LineSegment StartX=4.25 StartY=-21.3 StartZ=0 EndX=4.25 EndY=-18.5 EndZ=0
    g1: LineSegment StartX=4.25 StartY=-18.5 StartZ=0 EndX=17.75 EndY=-18.5 EndZ=0
    g2: LineSegment StartX=17.75 StartY=-18.5 StartZ=0 EndX=17.75 EndY=-21.3 EndZ=0
    g3: LineSegment StartX=17.75 StartY=-21.3 StartZ=0 EndX=16.25 EndY=-21.3 EndZ=0
    g4: LineSegment StartX=16.25 StartY=-21.3 StartZ=0 EndX=16.25 EndY=-20 EndZ=0
    g5: LineSegment StartX=16.25 StartY=-20 StartZ=0 EndX=5.75 EndY=-20 EndZ=0
    g6: LineSegment StartX=5.75 StartY=-20 StartZ=0 EndX=5.75 EndY=-21.3 EndZ=0
    g7: LineSegment StartX=5.75 StartY=-21.3 StartZ=0 EndX=4.25 EndY=-21.3 EndZ=0
  constraints (24):
    c: PointOnObject(g0,g-3)
    c: Vertical(g0)
    c: Coincident(g1,g0)
    c: Horizontal(g1)
    c: Coincident(g2,g1)
    c: PointOnObject(g2,g-3)
    c: Vertical(g2)
    c: Coincident(g3,g2)
    c: PointOnObject(g3,g-3)
    c: Coincident(g4,g3)
    c: Vertical(g4)
    c: Coincident(g5,g4)
    c: Horizontal(g5)
    c: Coincident(g6,g5)
    c: PointOnObject(g6,g-3)
    c: Vertical(g6)
    c: Coincident(g7,g6)
    c: Coincident(g7,g0)
    c: DistanceY(g6,g6) = 1.3
    c: DistanceY(g5,g0) = 1.5
    c: DistanceX(g0,g6) = 1.5
    c: DistanceX(g3,g2) = 1.5
    c: DistanceX(g6,g3) = 10.5
    c: DistanceX(g-4,g0) = 2.25
FEATURE [PartDesign::Pad] Pad050
  BaseFeature = -> Pad049
  Direction = (-9.4e-15,0,1)
  Length = 3
  Length2 = 10
  Profile = -> Sketch047
  ReferenceAxis = -> Sketch047 [N_Axis]
  Refine = true
  Suppressed = false
  Type = 0
FEATURE [Sketcher::SketchObject] Sketch048
  ArcFitTolerance = 1e-06
  AttachmentSupport = -> [Pad050]
  ExternalGeometry = -> [Pad050]
  FullyConstrained = true
  MakeInternals = false
  MapMode = 5
  Placement = pos=(1.114e-13,0,-12) rot=(1,0,0;3.14159rad)
  sketch-geometry (4):
    g0: LineSegment StartX=4 StartY=13 StartZ=0 EndX=18 EndY=13 EndZ=0
    g1: LineSegment StartX=18 StartY=13 StartZ=0 EndX=22 EndY=9 EndZ=0
    g2: LineSegment StartX=22 StartY=9 StartZ=0 EndX=0 EndY=9 EndZ=0
    g3: LineSegment StartX=0 StartY=9 StartZ=0 EndX=4 EndY=13 EndZ=0
  constraints (8):
    c: Coincident(g0,g-5)
    c: Coincident(g0,g-6)
    c: Coincident(g1,g0)
    c: Coincident(g1,g-6)
    c: Coincident(g2,g1)
    c: Coincident(g2,g-5)
    c: Coincident(g3,g2)
    c: Coincident(g3,g0)
FEATURE [PartDesign::Pocket] Pocket182
  BaseFeature = -> Pad050
  Direction = (-9.3e-15,0,1)
  Length = 1
  Length2 = 5
  Profile = -> Sketch048
  ReferenceAxis = -> Sketch048 [N_Axis]
  Refine = true
  Suppressed = false
  Type = 0
FEATURE [Sketcher::SketchObject] Sketch049
  ArcFitTolerance = 1e-06
  AttachmentSupport = -> [Pocket182]
  ExternalGeometry = -> [Pocket182]
  FullyConstrained = true
  MakeInternals = false
  MapMode = 5
  Placement = pos=(0,-21.3,0) rot=(1,0,0;1.5708rad)
  sketch-geometry (6):
    g0: LineSegment StartX=22 StartY=-11 StartZ=0 EndX=22 EndY=-12 EndZ=0
    g1: LineSegment StartX=22 StartY=-12 StartZ=0 EndX=14 EndY=-12 EndZ=0
    g2: LineSegment StartX=14 StartY=-12 StartZ=0 EndX=22 EndY=-11 EndZ=0
    g3: LineSegment StartX=1.724e-13 StartY=-12 StartZ=0 EndX=8 EndY=-12 EndZ=0
    g4: LineSegment StartX=8 StartY=-12 StartZ=0 EndX=1.581e-13 EndY=-11 EndZ=0
    g5: LineSegment StartX=1.581e-13 StartY=-11 StartZ=0 EndX=0 EndY=-12 EndZ=0
  constraints (16):
    c: PointOnObject(g0,g-5)
    c: Coincident(g0,g-5)
    c: Coincident(g1,g0)
    c: PointOnObject(g1,g-4)
    c: Coincident(g2,g1)
    c: Coincident(g3,g-4)
    c: PointOnObject(g3,g-4)
    c: Coincident(g4,g3)
    c: PointOnObject(g4,g-3)
    c: Coincident(g5,g4)
    c: Coincident(g5,g-4)
    c: Coincident(g2,g0)
    c: DistanceY(g0,g0) = 1
    c: DistanceY(g5,g5) = 1
    c: DistanceX(g3,g3) = 8
    c: DistanceX(g1,g1) = 8
FEATURE [PartDesign::Pocket] Pocket018
  BaseFeature = -> Pocket182
  Direction = (0,1,-2e-16)
  Length = 9
  Length2 = 5
  Profile = -> Sketch049
  ReferenceAxis = -> Sketch049 [N_Axis]
  Refine = true
  Suppressed = false
  Type = 0
FEATURE [Sketcher::SketchObject] Sketch050
  ArcFitTolerance = 1e-06
  AttachmentSupport = -> [Pocket018]
  FullyConstrained = true
  MakeInternals = false
  MapMode = 5
  Placement = pos=(1.114e-13,0,-12) rot=(1,0,0;3.14159rad)
  sketch-geometry (2):
    g0: Circle CenterX=4 CenterY=7.5 CenterZ=0 NormalX=0 NormalY=0 NormalZ=1 AngleXU=0 Radius=1.95
    g1: Circle CenterX=18 CenterY=7.5 CenterZ=0 NormalX=0 NormalY=0 NormalZ=1 AngleXU=0 Radius=1.95
  constraints (4):
    c: Coincident(g0,g-4)
    c: Coincident(g1,g-3)
    c: Diameter(g0) = 3.9
    c: Diameter(g1) = 3.9
FEATURE [PartDesign::Pocket] Pocket019
  BaseFeature = -> Pocket018
  Direction = (-9.3e-15,0,1)
  Length = 2.3
  Length2 = 5
  Profile = -> Sketch050
  ReferenceAxis = -> Sketch050 [N_Axis]
  Refine = true
  Suppressed = false
  Type = 0
FEATURE [Sketcher::SketchObject] Sketch051
  ArcFitTolerance = 1e-06
  AttachmentSupport = -> [Pocket019]
  ExternalGeometry = -> [Pocket019]
  FullyConstrained = true
  MakeInternals = false
  MapMode = 5
  Placement = pos=(1.69231,-3e-15,-13.5385) rot=(0.998068,0,0.062137;3.14159rad)
  sketch-geometry (8):
    g0: LineSegment StartX=14.0657 StartY=19.65 StartZ=0 EndX=14.0657 EndY=14.65 EndZ=0
    g1: LineSegment StartX=14.0657 StartY=14.65 StartZ=0 EndX=19.0657 EndY=14.65 EndZ=0
    g2: LineSegment StartX=19.0657 StartY=14.65 StartZ=0 EndX=19.0657 EndY=19.65 EndZ=0
    g3: LineSegment StartX=19.0657 StartY=19.65 StartZ=0 EndX=14.0657 EndY=19.65 EndZ=0
    g4: LineSegment StartX=14.5657 StartY=19.15 StartZ=0 EndX=14.5657 EndY=15.15 EndZ=0
    g5: LineSegment StartX=14.5657 StartY=15.15 StartZ=0 EndX=18.5657 EndY=15.15 EndZ=0
    g6: LineSegment StartX=18.5657 StartY=15.15 StartZ=0 EndX=18.5657 EndY=19.15 EndZ=0
    g7: LineSegment StartX=18.5657 StartY=19.15 StartZ=0 EndX=14.5657 EndY=19.15 EndZ=0
  constraints (24):
    c: Coincident(g0,g1)
    c: Coincident(g1,g2)
    c: Coincident(g2,g3)
    c: Coincident(g3,g0)
    c: Vertical(g0)
    c: Vertical(g2)
    c: Horizontal(g1)
    c: Horizontal(g3)
    c: Coincident(g4,g5)
    c: Coincident(g5,g6)
    c: Coincident(g6,g7)
    c: Coincident(g7,g4)
    c: Vertical(g4)
    c: Vertical(g6)
    c: Horizontal(g5)
    c: Horizontal(g7)
    c: DistanceX(g3,g3) = 5
    c: DistanceY(g0,g0) = 5
    c: DistanceY(g4,g4) = 4
    c: DistanceX(g5,g5) = 4
    c: DistanceX(g0,g4) = 0.5
    c: DistanceY(g1,g5) = 0.5
    c: DistanceX(g1,g-5) = 1.4
    c: DistanceY(g-5,g1) = 1.65
FEATURE [PartDesign::Pocket] Pocket020
  BaseFeature = -> Pocket019
  Direction = (-0.124035,0,0.992278)
  Length = 0.5
  Length2 = 5
  Profile = -> Sketch051
  ReferenceAxis = -> Sketch051 [N_Axis]
  Refine = true
  Suppressed = false
  Type = 0
FEATURE [Sketcher::SketchObject] Sketch052
  ArcFitTolerance = 1e-06
  AttachmentSupport = -> [Pocket020]
  ExternalGeometry = -> [Pocket020]
  FullyConstrained = true
  MakeInternals = false
  MapMode = 5
  Placement = pos=(-1.35385,-2.4e-15,-10.8308) rot=(0.998068,0,-0.062137;3.14159rad)
  sketch-geometry (8):
    g0: LineSegment StartX=2.76438 StartY=19.65 StartZ=0 EndX=2.76438 EndY=14.65 EndZ=0
    g1: LineSegment StartX=2.76438 StartY=14.65 StartZ=0 EndX=7.76438 EndY=14.65 EndZ=0
    g2: LineSegment StartX=7.76438 StartY=14.65 StartZ=0 EndX=7.76438 EndY=19.65 EndZ=0
    g3: LineSegment StartX=7.76438 StartY=19.65 StartZ=0 EndX=2.76438 EndY=19.65 EndZ=0
    g4: LineSegment StartX=3.26438 StartY=19.15 StartZ=0 EndX=3.26438 EndY=15.15 EndZ=0
    g5: LineSegment StartX=3.26438 StartY=15.15 StartZ=0 EndX=7.26438 EndY=15.15 EndZ=0
    g6: LineSegment StartX=7.26438 StartY=15.15 StartZ=0 EndX=7.26438 EndY=19.15 EndZ=0
    g7: LineSegment StartX=7.26438 StartY=19.15 StartZ=0 EndX=3.26438 EndY=19.15 EndZ=0
  constraints (24):
    c: Coincident(g0,g1)
    c: Coincident(g1,g2)
    c: Coincident(g2,g3)
    c: Coincident(g3,g0)
    c: Vertical(g0)
    c: Vertical(g2)
    c: Horizontal(g1)
    c: Horizontal(g3)
    c: Coincident(g4,g5)
    c: Coincident(g5,g6)
    c: Coincident(g6,g7)
    c: Coincident(g7,g4)
    c: Vertical(g4)
    c: Vertical(g6)
    c: Horizontal(g5)
    c: Horizontal(g7)
    c: DistanceY(g0,g-6) = 1.65
    c: DistanceY(g0,g0) = 5
    c: DistanceY(g4,g4) = 4
    c: DistanceX(g3,g3) = 5
    c: DistanceX(g7,g7) = 4
    c: DistanceX(g0,g4) = 0.5
    c: DistanceY(g0,g4) = 0.5
    c: DistanceX(g-6,g0) = 1.4
FEATURE [PartDesign::Pocket] Pocket021
  BaseFeature = -> Pocket020
  Direction = (0.124035,0,0.992278)
  Length = 0.5
  Length2 = 5
  Profile = -> Sketch052
  ReferenceAxis = -> Sketch052 [N_Axis]
  Refine = true
  Suppressed = false
  Type = 0
FEATURE [PartDesign::Body] Body004  label="Front Torso"
  AllowCompound = false
  Group = -> [Sketch031,Pad034,Sketch032,Pad035,Sketch033,Pad036,Sketch034,Pad037,Pad038,Sketch036,Pad042,Sketch037,Pad043,Sketch038,Pad044,Sketch039,Pad045,Sketch040,Pad046,Sketch041,Pocket178,Sketch042,Sketch043,Pocket179,Sketch044,Pad047,Sketch045,Pocket180,Pad048,Pocket181,Sketch046,Pad049,Sketch047,Pad050,Sketch048,Pocket182,Sketch049,Pocket018,Sketch050,Pocket019,Sketch051,Pocket020,Sketch052,Pocket021,+9 more]
  Origin = -> Origin005
  Placement = pos=(33,19,0) rot=(0,0,1;0rad)
  Tip = -> Pad053
COMPONENT P4 — recipe-attached ("Front Legs", modeled in this document).
Construction recipe (the document's own serialized feature program — sketch geometry with constraints, then the solid features built on it; lengths are millimeters unless a unit is written):

FEATURE [PartDesign::SubShapeBinder] Binder001
  BindCopyOnChange = 0
  BindMode = 2
  ClaimChildren = false
  Fuse = false
  MakeFace = true
  OffsetFill = false
  OffsetIntersection = false
  OffsetJoinType = 0
  OffsetOpenResult = false
  PartialLoad = false
  Refine = true
  Relative = true
  _Version = 2
FEATURE [Sketcher::SketchObject] Sketch057
  ArcFitTolerance = 1e-06
  AttachmentSupport = -> [Binder001]
  ExternalGeometry = -> [Binder001]
  FullyConstrained = true
  MakeInternals = false
  MapMode = 5
  Placement = pos=(5.68e-14,0,-6) rot=(0,0,1;0rad)
  sketch-geometry (4):
    g0: LineSegment StartX=4.1 StartY=-18.05 StartZ=0 EndX=4.1 EndY=-21.75 EndZ=0
    g1: LineSegment StartX=4.1 StartY=-21.75 StartZ=0 EndX=17.9 EndY=-21.75 EndZ=0
    g2: LineSegment StartX=17.9 StartY=-21.75 StartZ=0 EndX=17.9 EndY=-18.05 EndZ=0
    g3: LineSegment StartX=17.9 StartY=-18.05 StartZ=0 EndX=4.1 EndY=-18.05 EndZ=0
  constraints (13):
    c: Coincident(g0,g1)
    c: Coincident(g1,g2)
    c: Coincident(g2,g3)
    c: Coincident(g3,g0)
    c: Vertical(g0)
    c: Vertical(g2)
    c: Horizontal(g1)
    c: Horizontal(g3)
    c: DistanceX(g3,g3) = 13.8
    c: DistanceX(g-3,g2) = 0.15
    c: DistanceY(g-3,g-3) = 2.8
    c: DistanceY(g2,g2) = 3.7
    c: DistanceY(g-3,g2) = 0.45
FEATURE [PartDesign::Pad] Pad054
  Direction = (-9.5e-15,0,1)
  Length = 2
  Length2 = 10
  Profile = -> Sketch057
  ReferenceAxis = -> Sketch057 [N_Axis]
  Refine = true
  Suppressed = false
  Type = 0
FEATURE [Sketcher::SketchObject] Sketch058
  ArcFitTolerance = 1e-06
  AttachmentSupport = -> [Pad054]
  ExternalGeometry = -> [Pad054]
  FullyConstrained = true
  MakeInternals = false
  MapMode = 5
  Placement = pos=(3.78e-14,0,-4) rot=(0,0,1;0rad)
  sketch-geometry (29):
    g0: LineSegment StartX=2.8 StartY=-16.95 StartZ=0 EndX=7 EndY=-16.95 EndZ=0
    g1: LineSegment StartX=7 StartY=-16.95 StartZ=0 EndX=7 EndY=-13.05 EndZ=0
    g2: LineSegment StartX=7.5 StartY=-12.55 StartZ=0 EndX=14.5 EndY=-12.55 EndZ=0
    g3: LineSegment StartX=15 StartY=-13.05 StartZ=0 EndX=15 EndY=-16.95 EndZ=0
    g4: LineSegment StartX=15 StartY=-16.95 StartZ=0 EndX=19.2 EndY=-16.95 EndZ=0
    g5: LineSegment StartX=19.3 StartY=-58.45 StartZ=0 EndX=16.3 EndY=-58.45 EndZ=0
    g6: LineSegment StartX=15.8 StartY=-57.95 StartZ=0 EndX=15.8 EndY=-54.45 EndZ=0
    g7: LineSegment StartX=15.8 StartY=-54.45 StartZ=0 EndX=6.2 EndY=-54.45 EndZ=0
    g8: LineSegment StartX=6.2 StartY=-54.45 StartZ=0 EndX=6.2 EndY=-57.95 EndZ=0
    g9: LineSegment StartX=5.7 StartY=-58.45 StartZ=0 EndX=2.7 EndY=-58.45 EndZ=0
    g10: ArcOfCircle CenterX=2.8 CenterY=-17.45 CenterZ=0 NormalX=0 NormalY=0 NormalZ=1 AngleXU=0 Radius=0.5 StartAngle=1.5708 EndAngle=3.14159
    g11: ArcOfCircle CenterX=7.5 CenterY=-13.05 CenterZ=0 NormalX=0 NormalY=0 NormalZ=1 AngleXU=0 Radius=0.5 StartAngle=1.5708 EndAngle=3.14159
    g12: GeomPoint [constr] X=7 Y=-12.55 Z=0
    g13: ArcOfCircle CenterX=14.5 CenterY=-13.05 CenterZ=0 NormalX=0 NormalY=0 NormalZ=1 AngleXU=0 Radius=0.5 StartAngle=1.2e-15 EndAngle=1.5708
    g14: GeomPoint [constr] X=15 Y=-12.55 Z=0
    g15: ArcOfCircle CenterX=19.2 CenterY=-17.45 CenterZ=0 NormalX=0 NormalY=0 NormalZ=1 AngleXU=0 Radius=0.5 StartAngle=-9e-16 EndAngle=1.5708
    g16: ArcOfCircle CenterX=19.3 CenterY=-57.95 CenterZ=0 NormalX=0 NormalY=0 NormalZ=1 AngleXU=0 Radius=0.5 StartAngle=4.71239 EndAngle=6.28319
    g17: ArcOfCircle CenterX=16.3 CenterY=-57.95 CenterZ=0 NormalX=0 NormalY=0 NormalZ=1 AngleXU=0 Radius=0.5 StartAngle=3.14159 EndAngle=4.71239
    g18: GeomPoint [constr] X=15.8 Y=-58.45 Z=0
    g19: ArcOfCircle CenterX=5.7 CenterY=-57.95 CenterZ=0 NormalX=0 NormalY=0 NormalZ=1 AngleXU=0 Radius=0.5 StartAngle=4.71239 EndAngle=6.28319
    g20: GeomPoint [constr] X=6.2 Y=-58.45 Z=0
    g21: ArcOfCircle CenterX=2.7 CenterY=-57.95 CenterZ=0 NormalX=0 NormalY=0 NormalZ=1 AngleXU=0 Radius=0.5 StartAngle=3.14159 EndAngle=4.71239
    g22: GeomPoint [constr] X=2.7 Y=-58.45 Z=0
    g23: LineSegment StartX=2.3 StartY=-17.45 StartZ=0 EndX=2.3 EndY=-22.95 EndZ=0
    g24: LineSegment StartX=2.3 StartY=-22.95 StartZ=0 EndX=2.2 EndY=-22.95 EndZ=0
    g25: LineSegment StartX=2.2 StartY=-22.95 StartZ=0 EndX=2.2 EndY=-57.95 EndZ=0
    g26: LineSegment StartX=19.7 StartY=-17.45 StartZ=0 EndX=19.7 EndY=-22.95 EndZ=0
    g27: LineSegment StartX=19.7 StartY=-22.95 StartZ=0 EndX=19.8 EndY=-22.95 EndZ=0
    g28: LineSegment StartX=19.8 StartY=-22.95 StartZ=0 EndX=19.8 EndY=-57.95 EndZ=0
  constraints (77):
    c: Horizontal(g0)
    c: Coincident(g1,g0)
    c: Vertical(g1)
    c: Horizontal(g2)
    c: Vertical(g3)
    c: Coincident(g4,g3)
    c: Horizontal(g4)
    c: Horizontal(g5)
    c: Vertical(g6)
    c: Coincident(g7,g6)
    c: Horizontal(g7)
    c: Coincident(g8,g7)
    c: Vertical(g8)
    c: Horizontal(g9)
    c: DistanceY(g-3,g0) = 1.1
    c: DistanceY(g-3,g3) = 1.1
    c: DistanceX(g12,g14) = 8
    c: DistanceY(g20,g8) = 4
    c: DistanceY(g1,g12) = 4.4
    c: Tangent(g0,g10) = 1.5708
    c: Radius(g10) = 0.5
    c: PointOnObject(g12,g1)
    c: PointOnObject(g12,g2)
    c: Tangent(g1,g11) = 1.5708
    c: Tangent(g2,g11) = 1.5708
    c: PointOnObject(g14,g2)
    c: PointOnObject(g14,g3)
    c: Tangent(g2,g13) = 1.5708
    c: Tangent(g3,g13) = 1.5708
    c: Tangent(g4,g15) = 1.5708
    c: Tangent(g5,g16) = 1.5708
    c: PointOnObject(g18,g5)
    c: PointOnObject(g18,g6)
    c: Tangent(g5,g17) = 1.5708
    c: Tangent(g6,g17) = 1.5708
    c: PointOnObject(g20,g8)
    c: PointOnObject(g20,g9)
    c: Tangent(g8,g19) = 1.5708
    c: Tangent(g9,g19) = 1.5708
    c: Tangent(g9,g21) = 1.5708
    c: Radius(g21) = 0.5
    c: Radius(g19) = 0.5
    c: Radius(g17) = 0.5
    c: Radius(g16) = 0.5
    c: Radius(g15) = 0.5
    c: Radius(g13) = 0.5
    c: Radius(g11) = 0.5
    c: Coincident(g23,g10)
    c: Vertical(g23)
    c: Coincident(g24,g23)
    c: Horizontal(g24)
    c: Coincident(g25,g24)
    c: Vertical(g25)
    c: Coincident(g25,g21)
    c: DistanceY(g23,g0) = 6
    c: DistanceX(g24,g24) = 0.1
    c: DistanceX(g21,g8) = 4
    c: Coincident(g22,g9)
    c: Coincident(g26,g15)
    c: Vertical(g26)
    c: Coincident(g27,g26)
    c: Horizontal(g27)
    c: Coincident(g28,g27)
    c: Coincident(g28,g16)
    c: Vertical(g28)
    c: DistanceX(g6,g16) = 4
    c: DistanceX(g27,g27) = 0.1
    c: DistanceY(g26,g4) = 6
    c: DistanceX(g21,g16) = 17.6
    c: DistanceY(g5,g6) = 4
    c: DistanceX(g-3,g15) = 1.8
    c: DistanceX(g3,g15) = 4.7
    c: DistanceY(g15,g15) = 0
    c: DistanceY(g10,g10) = 0
    c: DistanceY(g9,g0) = 41.5
    c: DistanceY(g16,g16) = 0
    c: DistanceY(g21,g21) = 0
FEATURE [PartDesign::Pad] Pad055
  BaseFeature = -> Pad054
  Direction = (-9.5e-15,0,1)
  Length = 4.8
  Length2 = 10
  Profile = -> Sketch058
  ReferenceAxis = -> Sketch058 [N_Axis]
  Refine = true
  Reversed = true
  Suppressed = false
  Type = 0
FEATURE [Sketcher::SketchObject] Sketch059
  ArcFitTolerance = 1e-06
  AttachmentSupport = -> [Pad054]
  ExternalGeometry = -> [Pad054]
  FullyConstrained = true
  MakeInternals = false
  MapMode = 5
  Placement = pos=(5.68e-14,0,-6) rot=(1,0,0;3.14159rad)
  sketch-geometry (4):
    g0: LineSegment StartX=4.1 StartY=21.75 StartZ=0 EndX=4.1 EndY=18.05 EndZ=0
    g1: LineSegment StartX=4.1 StartY=18.05 StartZ=0 EndX=17.9 EndY=18.05 EndZ=0
    g2: LineSegment StartX=17.9 StartY=18.05 StartZ=0 EndX=17.9 EndY=21.75 EndZ=0
    g3: LineSegment StartX=17.9 StartY=21.75 StartZ=0 EndX=4.1 EndY=21.75 EndZ=0
  constraints (10):
    c: Coincident(g0,g1)
    c: Coincident(g1,g2)
    c: Coincident(g2,g3)
    c: Coincident(g3,g0)
    c: Vertical(g0)
    c: Vertical(g2)
    c: Horizontal(g1)
    c: Horizontal(g3)
    c: Coincident(g0,g-3)
    c: Coincident(g1,g-4)
FEATURE [PartDesign::Pocket] Pocket023
  BaseFeature = -> Pad055
  Direction = (-9.5e-15,0,1)
  Length = 5
  Length2 = 5
  Profile = -> Sketch059
  ReferenceAxis = -> Sketch059 [N_Axis]
  Refine = true
  Reversed = true
  Suppressed = false
  Type = 0
FEATURE [Sketcher::SketchObject] Sketch060
  ArcFitTolerance = 1e-06
  AttachmentSupport = -> [Pocket023]
  ExternalGeometry = -> [Pocket023]
  FullyConstrained = true
  MakeInternals = false
  MapMode = 5
  Placement = pos=(8.32e-14,0,-8.8) rot=(1,0,0;3.14159rad)
  sketch-geometry (4):
    g0: LineSegment StartX=8.1 StartY=46.35 StartZ=0 EndX=8.1 EndY=30.35 EndZ=0
    g1: LineSegment StartX=8.1 StartY=30.35 StartZ=0 EndX=13.9 EndY=30.35 EndZ=0
    g2: LineSegment StartX=13.9 StartY=30.35 StartZ=0 EndX=13.9 EndY=46.35 EndZ=0
    g3: LineSegment StartX=13.9 StartY=46.35 StartZ=0 EndX=8.1 EndY=46.35 EndZ=0
  constraints (12):
    c: Coincident(g0,g1)
    c: Coincident(g1,g2)
    c: Coincident(g2,g3)
    c: Coincident(g3,g0)
    c: Vertical(g0)
    c: Vertical(g2)
    c: Horizontal(g1)
    c: Horizontal(g3)
    c: DistanceX(g3,g3) = 5.8
    c: DistanceY(g2,g-3) = 8.1
    c: DistanceY(g-4,g1) = 8.6
    c: DistanceX(g-6,g0) = 5.8
FEATURE [PartDesign::Pocket] Pocket024
  BaseFeature = -> Pocket023
  Direction = (-9.5e-15,0,1)
  Length = 5
  Length2 = 5
  Profile = -> Sketch060
  ReferenceAxis = -> Sketch060 [N_Axis]
  Refine = true
  Suppressed = false
  Type = 0
FEATURE [Sketcher::SketchObject] Sketch061
  ArcFitTolerance = 1e-06
  AttachmentSupport = -> [Pocket024]
  ExternalGeometry = -> [Pocket024]
  FullyConstrained = true
  MakeInternals = false
  MapMode = 5
  Placement = pos=(8.32e-14,0,-8.8) rot=(1,0,0;3.14159rad)
  sketch-geometry (8):
    g0: ArcOfCircle CenterX=18.65 CenterY=18.8 CenterZ=0 NormalX=0 NormalY=0 NormalZ=1 AngleXU=0 Radius=0.75 StartAngle=3.14159 EndAngle=6.28319
    g1: ArcOfCircle CenterX=18.65 CenterY=57.7 CenterZ=0 NormalX=0 NormalY=0 NormalZ=1 AngleXU=0 Radius=0.75 StartAngle=0 EndAngle=3.14159
    g2: LineSegment StartX=17.9 StartY=18.8 StartZ=0 EndX=17.9 EndY=57.7 EndZ=0
    g3: LineSegment StartX=19.4 StartY=18.8 StartZ=0 EndX=19.4 EndY=57.7 EndZ=0
    g4: ArcOfCircle CenterX=3.35 CenterY=57.7 CenterZ=0 NormalX=0 NormalY=0 NormalZ=1 AngleXU=0 Radius=0.75 StartAngle=-3.217e-12 EndAngle=3.14159
    g5: ArcOfCircle CenterX=3.35 CenterY=18.8 CenterZ=0 NormalX=0 NormalY=0 NormalZ=1 AngleXU=0 Radius=0.75 StartAngle=3.14159 EndAngle=6.28319
    g6: LineSegment StartX=4.1 StartY=57.7 StartZ=0 EndX=4.1 EndY=18.8 EndZ=0
    g7: LineSegment StartX=2.6 StartY=57.7 StartZ=0 EndX=2.6 EndY=18.8 EndZ=0
  constraints (20):
    c: Tangent(g0,g2) = 1.5708
    c: Tangent(g0,g3) = -1.5708
    c: Tangent(g1,g2) = 1.5708
    c: Tangent(g1,g3) = -1.5708
    c: Equal(g0,g1)
    c: Vertical(g2)
    c: Tangent(g4,g6) = 1.5708
    c: Tangent(g4,g7) = -1.5708
    c: Tangent(g5,g6) = 1.5708
    c: Tangent(g5,g7) = -1.5708
    c: Equal(g4,g5)
    c: Vertical(g6)
    c: PointOnObject(g0,g-3)
    c: Diameter(g0) = 1.5
    c: Diameter(g5) = 1.5
    c: PointOnObject(g5,g-4)
    c: DistanceY(g-4,g5) = 0.75
    c: DistanceY(g-3,g0) = 0.75
    c: DistanceY(g1,g-6) = 0.75
    c: DistanceY(g4,g-5) = 0.75
FEATURE [PartDesign::Pad] Pad056
  BaseFeature = -> Pocket024
  Direction = (9.5e-15,0,-1)
  Length = 0.2
  Length2 = 10
  Profile = -> Sketch061
  ReferenceAxis = -> Sketch061 [N_Axis]
  Refine = true
  Suppressed = false
  Type = 0
FEATURE [Sketcher::SketchObject] Sketch062
  ArcFitTolerance = 1e-06
  AttachmentSupport = -> [Pad056]
  ExternalGeometry = -> [Pad056]
  FullyConstrained = true
  MakeInternals = false
  MapMode = 5
  Placement = pos=(8.46e-14,0,-9) rot=(1,0,0;3.14159rad)
  sketch-geometry (8):
    g0: ArcOfCircle CenterX=3.35 CenterY=56.7 CenterZ=0 NormalX=0 NormalY=0 NormalZ=1 AngleXU=0 Radius=0.25 StartAngle=-3.6e-15 EndAngle=3.14159
    g1: ArcOfCircle CenterX=3.35 CenterY=45.7 CenterZ=0 NormalX=0 NormalY=0 NormalZ=1 AngleXU=0 Radius=0.25 StartAngle=3.14159 EndAngle=6.28319
    g2: LineSegment StartX=3.6 StartY=56.7 StartZ=0 EndX=3.6 EndY=45.7 EndZ=0
    g3: LineSegment StartX=3.1 StartY=56.7 StartZ=0 EndX=3.1 EndY=45.7 EndZ=0
    g4: ArcOfCircle CenterX=18.65 CenterY=56.7 CenterZ=0 NormalX=0 NormalY=0 NormalZ=1 AngleXU=0 Radius=0.25 StartAngle=1.28e-14 EndAngle=3.14159
    g5: ArcOfCircle CenterX=18.65 CenterY=45.7 CenterZ=0 NormalX=0 NormalY=0 NormalZ=1 AngleXU=0 Radius=0.25 StartAngle=3.14159 EndAngle=6.28319
    g6: LineSegment StartX=18.9 StartY=56.7 StartZ=0 EndX=18.9 EndY=45.7 EndZ=0
    g7: LineSegment StartX=18.4 StartY=56.7 StartZ=0 EndX=18.4 EndY=45.7 EndZ=0
  constraints (20):
    c: Tangent(g0,g2) = 1.5708
    c: Tangent(g0,g3) = -1.5708
    c: Tangent(g1,g2) = 1.5708
    c: Tangent(g1,g3) = -1.5708
    c: Equal(g0,g1)
    c: Vertical(g2)
    c: Tangent(g4,g6) = 1.5708
    c: Tangent(g4,g7) = -1.5708
    c: Tangent(g5,g6) = 1.5708
    c: Tangent(g5,g7) = -1.5708
    c: Equal(g4,g5)
    c: Vertical(g6)
    c: DistanceY(g1,g0) = 11
    c: DistanceY(g5,g4) = 11
    c: DistanceY(g4,g-4) = 1
    c: DistanceY(g0,g-3) = 1
    c: DistanceX(g0,g-3) = 0
    c: DistanceX(g-4,g4) = 0
    c: Diameter(g4) = 0.5
    c: Diameter(g0) = 0.5
FEATURE [PartDesign::Pad] Pad057
  BaseFeature = -> Pad056
  Direction = (9.4e-15,0,-1)
  Length = 0.2
  Length2 = 10
  Profile = -> Sketch062
  ReferenceAxis = -> Sketch062 [N_Axis]
  Refine = true
  Suppressed = false
  Type = 0
FEATURE [Sketcher::SketchObject] Sketch063
  ArcFitTolerance = 1e-06
  AttachmentSupport = -> [Pad057]
  ExternalGeometry = -> [Pad057]
  FullyConstrained = true
  MakeInternals = false
  MapMode = 5
  Placement = pos=(8.32e-14,0,-8.8) rot=(1,0,0;3.14159rad)
  sketch-geometry (8):
    g0: LineSegment StartX=8.1 StartY=46.35 StartZ=0 EndX=13.9 EndY=46.35 EndZ=0
    g1: LineSegment StartX=13.9 StartY=46.35 StartZ=0 EndX=13.9 EndY=54.45 EndZ=0
    g2: LineSegment StartX=13.9 StartY=54.45 StartZ=0 EndX=8.1 EndY=54.45 EndZ=0
    g3: LineSegment StartX=8.1 StartY=54.45 StartZ=0 EndX=8.1 EndY=46.35 EndZ=0
    g4: LineSegment StartX=8.1 StartY=30.35 StartZ=0 EndX=8.1 EndY=21.75 EndZ=0
    g5: LineSegment StartX=8.1 StartY=21.75 StartZ=0 EndX=13.9 EndY=21.75 EndZ=0
    g6: LineSegment StartX=13.9 StartY=21.75 StartZ=0 EndX=13.9 EndY=30.35 EndZ=0
    g7: LineSegment StartX=13.9 StartY=30.35 StartZ=0 EndX=8.1 EndY=30.35 EndZ=0
  constraints (20):
    c: Coincident(g0,g1)
    c: Coincident(g1,g2)
    c: Coincident(g2,g3)
    c: Coincident(g3,g0)
    c: Horizontal(g2)
    c: Vertical(g1)
    c: Vertical(g3)
    c: Coincident(g0,g-4)
    c: PointOnObject(g1,g-3)
    c: Coincident(g4,g5)
    c: Coincident(g5,g6)
    c: Coincident(g6,g7)
    c: Coincident(g7,g4)
    c: Vertical(g4)
    c: Vertical(g6)
    c: Horizontal(g5)
    c: Coincident(g4,g-5)
    c: PointOnObject(g5,g-6)
    c: Coincident(g6,g-5)
    c: Coincident(g0,g-4)
FEATURE [PartDesign::Pocket] Pocket025
  BaseFeature = -> Pad057
  Direction = (-9.5e-15,0,1)
  Length = 1
  Length2 = 5
  Profile = -> Sketch063
  ReferenceAxis = -> Sketch063 [N_Axis]
  Refine = true
  Suppressed = false
  Type = 0
FEATURE [PartDesign::Fillet] Fillet031
  Base = -> Pocket025 [Edge78,Edge80]
  BaseFeature = -> Pocket025
  Radius = 1
  Refine = true
  SupportTransform = false
  Suppressed = false
  UseAllEdges = false
FEATURE [Sketcher::SketchObject] Sketch064
  ArcFitTolerance = 1e-06
  AttachmentSupport = -> [Fillet031]
  ExternalGeometry = -> [Fillet031]
  FullyConstrained = true
  MakeInternals = false
  MapMode = 5
  Placement = pos=(7.4e-14,0,-7.8) rot=(1,0,0;3.14159rad)
  sketch-geometry (2):
    g0: Circle CenterX=11 CenterY=50.4 CenterZ=0 NormalX=0 NormalY=0 NormalZ=1 AngleXU=0 Radius=1.95
    g1: Circle CenterX=11 CenterY=26.05 CenterZ=0 NormalX=0 NormalY=0 NormalZ=1 AngleXU=0 Radius=1.95
  constraints (12):
    c: DistanceX(g-5,g-5) = 5.8
    c: DistanceX(g-5,g1) = 2.9
    c: DistanceY(g-3,g-5) = 8.6
    c: DistanceY(g-5,g-5) = 0
    c: DistanceY(g1,g-5) = 4.3
    c: Diameter(g1) = 3.9
    c: DistanceX(g-6,g-6) = 5.8
    c: DistanceY(g-6,g-7) = 8.1
    c: DistanceX(g-3,g-3) = 0
    c: DistanceX(g0,g-6) = 2.9
    c: DistanceY(g0,g-7) = 4.05
    c: Diameter(g0) = 3.9
FEATURE [PartDesign::Pocket] Pocket026
  BaseFeature = -> Fillet031
  Direction = (-9.5e-15,0,1)
  Length = 1.5
  Length2 = 5
  Profile = -> Sketch064
  ReferenceAxis = -> Sketch064 [N_Axis]
  Refine = true
  Suppressed = false
  Type = 0
FEATURE [Sketcher::SketchObject] Sketch065
  ArcFitTolerance = 1e-06
  AttachmentSupport = -> [Pocket026]
  ExternalGeometry = -> [Pocket026]
  FullyConstrained = true
  MakeInternals = false
  MapMode = 5
  Placement = pos=(5.93e-14,0,-6.3) rot=(1,0,0;3.14159rad)
  sketch-geometry (2):
    g0: Circle CenterX=11 CenterY=50.4 CenterZ=0 NormalX=0 NormalY=0 NormalZ=1 AngleXU=0 Radius=1
    g1: Circle CenterX=11 CenterY=26.05 CenterZ=0 NormalX=0 NormalY=0 NormalZ=1 AngleXU=0 Radius=1
  constraints (4):
    c: Coincident(g0,g-3)
    c: Coincident(g1,g-4)
    c: Diameter(g1) = 2
    c: Diameter(g0) = 2
FEATURE [PartDesign::Pocket] Pocket027
  BaseFeature = -> Pocket026
  Direction = (-9.4e-15,0,1)
  Length = 5
  Length2 = 5
  Profile = -> Sketch065
  ReferenceAxis = -> Sketch065 [N_Axis]
  Refine = true
  Suppressed = false
  Type = 0
FEATURE [Sketcher::SketchObject] Sketch066
  ArcFitTolerance = 1e-06
  AttachmentSupport = -> [Pocket027]
  ExternalGeometry = -> [Pocket027]
  FullyConstrained = true
  MakeInternals = false
  MapMode = 5
  Placement = pos=(3.78e-14,0,-4) rot=(0,0,1;0rad)
  sketch-geometry (20):
    g0: LineSegment StartX=8.5 StartY=-14.35 StartZ=0 EndX=8.5 EndY=-17.65 EndZ=0
    g1: LineSegment StartX=8.5 StartY=-17.65 StartZ=0 EndX=13.5 EndY=-17.65 EndZ=0
    g2: LineSegment StartX=13.5 StartY=-17.65 StartZ=0 EndX=13.5 EndY=-14.35 EndZ=0
    g3: LineSegment StartX=13.5 StartY=-14.35 StartZ=0 EndX=8.5 EndY=-14.35 EndZ=0
    g4: LineSegment StartX=3.9 StartY=-24.15 StartZ=0 EndX=3.9 EndY=-56.95 EndZ=0
    g5: LineSegment StartX=3.9 StartY=-56.95 StartZ=0 EndX=4.7 EndY=-56.95 EndZ=0
    g6: LineSegment StartX=4.7 StartY=-56.95 StartZ=0 EndX=4.7 EndY=-53.75 EndZ=0
    g7: LineSegment StartX=5.2 StartY=-53.25 StartZ=0 EndX=6.4 EndY=-53.25 EndZ=0
    g8: LineSegment StartX=6.4 StartY=-53.25 StartZ=0 EndX=6.4 EndY=-24.15 EndZ=0
    g9: LineSegment StartX=6.4 StartY=-24.15 StartZ=0 EndX=3.9 EndY=-24.15 EndZ=0
    g10: LineSegment StartX=18.1 StartY=-24.15 StartZ=0 EndX=15.6 EndY=-24.15 EndZ=0
    g11: LineSegment StartX=15.6 StartY=-24.15 StartZ=0 EndX=15.6 EndY=-53.25 EndZ=0
    g12: LineSegment StartX=15.6 StartY=-53.25 StartZ=0 EndX=16.8 EndY=-53.25 EndZ=0
    g13: LineSegment StartX=17.3 StartY=-53.75 StartZ=0 EndX=17.3 EndY=-56.95 EndZ=0
    g14: LineSegment StartX=17.3 StartY=-56.95 StartZ=0 EndX=18.1 EndY=-56.95 EndZ=0
    g15: LineSegment StartX=18.1 StartY=-56.95 StartZ=0 EndX=18.1 EndY=-24.15 EndZ=0
    g16: ArcOfCircle CenterX=5.2 CenterY=-53.75 CenterZ=0 NormalX=0 NormalY=0 NormalZ=1 AngleXU=0 Radius=0.5 StartAngle=1.5708 EndAngle=3.14159
    g17: GeomPoint [constr] X=4.7 Y=-53.25 Z=0
    g18: ArcOfCircle CenterX=16.8 CenterY=-53.75 CenterZ=0 NormalX=0 NormalY=0 NormalZ=1 AngleXU=0 Radius=0.5 StartAngle=5.4e-15 EndAngle=1.5708
    g19: GeomPoint [constr] X=17.3 Y=-53.25 Z=0
  constraints (56):
    c: Coincident(g0,g1)
    c: Coincident(g1,g2)
    c: Coincident(g2,g3)
    c: Coincident(g3,g0)
    c: Vertical(g0)
    c: Vertical(g2)
    c: Horizontal(g1)
    c: Horizontal(g3)
    c: DistanceY(g0,g-3) = 1.8
    c: DistanceX(g-4,g0) = 1.5
    c: DistanceX(g2,g-5) = 1.5
    c: DistanceY(g0,g0) = 3.3
    c: Vertical(g4)
    c: Coincident(g5,g4)
    c: Horizontal(g5)
    c: Coincident(g6,g5)
    c: Vertical(g6)
    c: Horizontal(g7)
    c: Coincident(g8,g7)
    c: Vertical(g8)
    c: Coincident(g9,g8)
    c: Coincident(g9,g4)
    c: Horizontal(g9)
    c: Horizontal(g10)
    c: Coincident(g11,g10)
    c: Vertical(g11)
    c: Coincident(g12,g11)
    c: Horizontal(g12)
    c: Coincident(g14,g13)
    c: Horizontal(g14)
    c: Coincident(g15,g14)
    c: Coincident(g15,g10)
    c: Vertical(g15)
    c: Vertical(g13)
    c: PointOnObject(g17,g6)
    c: PointOnObject(g17,g7)
    c: Tangent(g6,g16) = 1.5708
    c: Tangent(g7,g16) = 1.5708
    c: PointOnObject(g19,g12)
    c: PointOnObject(g19,g13)
    c: Tangent(g12,g18) = 1.5708
    c: Tangent(g13,g18) = 1.5708
    c: Radius(g18) = 0.5
    c: Radius(g16) = 0.5
    c: DistanceX(g9,g9) = 2.5
    c: DistanceX(g10,g10) = 2.5
    c: DistanceX(g-7,g4) = 1.6
    c: DistanceX(g10,g-6) = 1.6
    c: DistanceY(g4,g-10) = 7.2
    c: DistanceY(g10,g-11) = 7.2
    c: DistanceY(g-13,g5) = 1.5
    c: DistanceX(g5,g-12) = 1.5
    c: DistanceX(g-15,g13) = 1.5
    c: DistanceY(g-16,g13) = 1.5
    c: DistanceY(g-12,g7) = 1.2
    c: DistanceY(g-15,g11) = 1.2
FEATURE [PartDesign::Pocket] Pocket028
  BaseFeature = -> Pocket027
  Direction = (9.5e-15,0,-1)
  Length = 3.5
  Length2 = 5
  Profile = -> Sketch066
  ReferenceAxis = -> Sketch066 [N_Axis]
  Refine = true
  Suppressed = false
  Type = 0
FEATURE [Sketcher::SketchObject] Sketch067
  ArcFitTolerance = 1e-06
  AttachmentSupport = -> [Pocket028]
  ExternalGeometry = -> [Pocket028]
  FullyConstrained = true
  MakeInternals = false
  MapMode = 5
  Placement = pos=(3.78e-14,0,-4) rot=(0,0,1;0rad)
  sketch-geometry (8):
    g0: LineSegment StartX=6.2 StartY=-54.45 StartZ=0 EndX=2.2 EndY=-54.45 EndZ=0
    g1: LineSegment StartX=2.2 StartY=-54.45 StartZ=0 EndX=2.2 EndY=-58.45 EndZ=0
    g2: LineSegment StartX=2.2 StartY=-58.45 StartZ=0 EndX=6.2 EndY=-58.45 EndZ=0
    g3: LineSegment StartX=6.2 StartY=-58.45 StartZ=0 EndX=6.2 EndY=-54.45 EndZ=0
    g4: LineSegment StartX=15.8 StartY=-54.45 StartZ=0 EndX=15.8 EndY=-58.45 EndZ=0
    g5: LineSegment StartX=15.8 StartY=-58.45 StartZ=0 EndX=19.8 EndY=-58.45 EndZ=0
    g6: LineSegment StartX=19.8 StartY=-58.45 StartZ=0 EndX=19.8 EndY=-54.45 EndZ=0
    g7: LineSegment StartX=19.8 StartY=-54.45 StartZ=0 EndX=15.8 EndY=-54.45 EndZ=0
  constraints (22):
    c: Coincident(g0,g1)
    c: Coincident(g1,g2)
    c: Coincident(g2,g3)
    c: Coincident(g3,g0)
    c: Horizontal(g0)
    c: Horizontal(g2)
    c: Vertical(g1)
    c: Vertical(g3)
    c: Coincident(g0,g-7)
    c: Coincident(g4,g5)
    c: Coincident(g5,g6)
    c: Coincident(g6,g7)
    c: Coincident(g7,g4)
    c: Vertical(g4)
    c: Vertical(g6)
    c: Horizontal(g5)
    c: Horizontal(g7)
    c: Coincident(g4,g-7)
    c: DistanceY(g4,g-5) = 0
    c: DistanceY(g2,g-6) = 0
    c: DistanceX(g1,g-3) = 0
    c: DistanceX(g-4,g5) = 0
FEATURE [PartDesign::Pocket] Pocket029
  BaseFeature = -> Pocket028
  Direction = (9.5e-15,0,-1)
  Length = 1
  Length2 = 5
  Profile = -> Sketch067
  ReferenceAxis = -> Sketch067 [N_Axis]
  Refine = true
  Suppressed = false
  Type = 0
FEATURE [Sketcher::SketchObject] Sketch068
  ArcFitTolerance = 1e-06
  AttachmentSupport = -> [Pocket029]
  ExternalGeometry = -> [Pocket029]
  FullyConstrained = true
  MakeInternals = false
  MapMode = 5
  Placement = pos=(3.78e-14,0,-4) rot=(0,0,1;0rad)
  sketch-geometry (2):
    g0: Circle CenterX=11 CenterY=-50.4 CenterZ=0 NormalX=0 NormalY=0 NormalZ=1 AngleXU=0 Radius=2
    g1: Circle CenterX=11 CenterY=-26.05 CenterZ=0 NormalX=0 NormalY=0 NormalZ=1 AngleXU=0 Radius=2
  constraints (4):
    c: Coincident(g0,g-4)
    c: Coincident(g1,g-3)
    c: Diameter(g1) = 4
    c: Diameter(g0) = 4
FEATURE [PartDesign::Pocket] Pocket030
  BaseFeature = -> Pocket029
  Direction = (9.5e-15,0,-1)
  Length = 1.7
  Length2 = 5
  Profile = -> Sketch068
  ReferenceAxis = -> Sketch068 [N_Axis]
  Refine = true
  Suppressed = false
  Type = 0
FEATURE [Sketcher::SketchObject] Sketch069
  ArcFitTolerance = 1e-06
  AttachmentSupport = -> [Pocket030]
  ExternalGeometry = -> [Pocket030]
  FullyConstrained = true
  MakeInternals = false
  MapMode = 5
  Placement = pos=(19.8,0,1.873e-13) rot=(0.57735,0.57735,0.57735;2.0944rad)
  sketch-geometry (4):
    g0: ArcOfCircle CenterX=-48.25 CenterY=-4 CenterZ=0 NormalX=0 NormalY=0 NormalZ=1 AngleXU=0 Radius=2.2 StartAngle=3.14159 EndAngle=4.71239
    g1: ArcOfCircle CenterX=-29.35 CenterY=-4 CenterZ=0 NormalX=0 NormalY=0 NormalZ=1 AngleXU=0 Radius=2.2 StartAngle=4.71239 EndAngle=6.28319
    g2: LineSegment StartX=-50.45 StartY=-4 StartZ=0 EndX=-27.15 EndY=-4 EndZ=0
    g3: LineSegment StartX=-29.35 StartY=-6.2 StartZ=0 EndX=-48.25 EndY=-6.2 EndZ=0
  constraints (14):
    c: PointOnObject(g0,g-3)
    c: PointOnObject(g1,g-3)
    c: Coincident(g2,g0)
    c: Coincident(g2,g1)
    c: Coincident(g3,g1)
    c: Coincident(g3,g0)
    c: Horizontal(g3)
    c: Radius(g1) = 2.2
    c: Radius(g0) = 2.2
    c: DistanceY(g0,g-3) = 2.2
    c: DistanceX(g1,g1) = 0
    c: DistanceX(g0,g0) = 0
    c: DistanceX(g-3,g0) = 4
    c: DistanceX(g0,g1) = 23.3
FEATURE [PartDesign::Pocket] Pocket031
  BaseFeature = -> Pocket030
  Direction = (-1,-1e-16,-9.4e-15)
  Length = 2
  Length2 = 5
  Profile = -> Sketch069
  ReferenceAxis = -> Sketch069 [N_Axis]
  Refine = true
  Suppressed = false
  Type = 0
FEATURE [Sketcher::SketchObject] Sketch070
  ArcFitTolerance = 1e-06
  AttachmentSupport = -> [Pocket031]
  ExternalGeometry = -> [Pocket031]
  FullyConstrained = true
  MakeInternals = false
  MapMode = 5
  Placement = pos=(2.2,0,2.08e-14) rot=(0.57735,-0.57735,-0.57735;2.0944rad)
  sketch-geometry (4):
    g0: ArcOfCircle CenterX=29.35 CenterY=-4 CenterZ=0 NormalX=0 NormalY=0 NormalZ=1 AngleXU=0 Radius=2.2 StartAngle=3.14159 EndAngle=4.71239
    g1: ArcOfCircle CenterX=48.25 CenterY=-4 CenterZ=0 NormalX=0 NormalY=0 NormalZ=1 AngleXU=0 Radius=2.2 StartAngle=4.71239 EndAngle=6.28319
    g2: LineSegment StartX=27.15 StartY=-4 StartZ=0 EndX=50.45 EndY=-4 EndZ=0
    g3: LineSegment StartX=48.25 StartY=-6.2 StartZ=0 EndX=29.35 EndY=-6.2 EndZ=0
  constraints (14):
    c: PointOnObject(g0,g-3)
    c: PointOnObject(g1,g-3)
    c: Coincident(g2,g0)
    c: Coincident(g2,g1)
    c: Coincident(g3,g1)
    c: Coincident(g3,g0)
    c: Horizontal(g3)
    c: DistanceX(g1,g-3) = 4
    c: DistanceX(g0,g1) = 23.3
    c: Radius(g0) = 2.2
    c: Radius(g1) = 2.2
    c: DistanceY(g1,g1) = 2.2
    c: DistanceX(g0,g0) = 0
    c: DistanceX(g1,g1) = 0
FEATURE [PartDesign::Pocket] Pocket032
  BaseFeature = -> Pocket031
  Direction = (1,-1e-16,9.4e-15)
  Length = 2
  Length2 = 5
  Profile = -> Sketch070
  ReferenceAxis = -> Sketch070 [N_Axis]
  Refine = true
  Suppressed = false
  Type = 0
FEATURE [Sketcher::SketchObject] Sketch187
  ArcFitTolerance = 1e-06
  AttachmentSupport = -> [Pocket032]
  ExternalGeometry = -> [Pocket032]
  FullyConstrained = true
  MakeInternals = false
  MapMode = 5
  Placement = pos=(5.68e-14,0,-6) rot=(1,0,0;3.14159rad)
  sketch-geometry (4):
    g0: LineSegment StartX=4.1 StartY=18.05 StartZ=0 EndX=17.9 EndY=18.05 EndZ=0
    g1: LineSegment StartX=17.9 StartY=18.05 StartZ=0 EndX=17.9 EndY=18.9 EndZ=0
    g2: LineSegment StartX=17.9 StartY=18.9 StartZ=0 EndX=4.1 EndY=18.9 EndZ=0
    g3: LineSegment StartX=4.1 StartY=18.9 StartZ=0 EndX=4.1 EndY=18.05 EndZ=0
  constraints (11):
    c: Coincident(g0,g1)
    c: Coincident(g1,g2)
    c: Coincident(g2,g3)
    c: Coincident(g3,g0)
    c: Horizontal(g0)
    c: Horizontal(g2)
    c: Vertical(g1)
    c: Vertical(g3)
    c: Coincident(g0,g-5)
    c: PointOnObject(g1,g-4)
    c: DistanceY(g1,g1) = 0.85
FEATURE [PartDesign::Pad] Pad137
  BaseFeature = -> Pocket032
  Direction = (9.5e-15,0,-1)
  Length = 2.8
  Length2 = 10
  Profile = -> Sketch187
  ReferenceAxis = -> Sketch187 [N_Axis]
  Refine = true
  Suppressed = false
  Type = 0
FEATURE [Sketcher::SketchObject] Sketch301
  ArcFitTolerance = 1e-06
  AttachmentSupport = -> [Pad137]
  ExternalGeometry = -> [Pad137]
  FullyConstrained = true
  MakeInternals = false
  MapMode = 5
  Placement = pos=(8.66e-14,0,-9.2) rot=(1,0,0;3.14159rad)
  sketch-geometry (4):
    g0: LineSegment StartX=2.6 StartY=57.7 StartZ=0 EndX=2.6 EndY=45.2 EndZ=0
    g1: LineSegment StartX=2.6 StartY=45.2 StartZ=0 EndX=19.4 EndY=45.2 EndZ=0
    g2: LineSegment StartX=19.4 StartY=45.2 StartZ=0 EndX=19.4 EndY=57.7 EndZ=0
    g3: LineSegment StartX=19.4 StartY=57.7 StartZ=0 EndX=2.6 EndY=57.7 EndZ=0
  constraints (11):
    c: Coincident(g0,g1)
    c: Coincident(g1,g2)
    c: Coincident(g2,g3)
    c: Coincident(g3,g0)
    c: Vertical(g0)
    c: Vertical(g2)
    c: Horizontal(g1)
    c: Horizontal(g3)
    c: Coincident(g0,g-3)
    c: PointOnObject(g1,g-4)
    c: DistanceY(g2,g2) = 12.5
FEATURE [PartDesign::Pocket] Pocket085
  BaseFeature = -> Pad137
  Direction = (-9.4e-15,0,1)
  Length = 0.2
  Length2 = 5
  Profile = -> Sketch301
  ReferenceAxis = -> Sketch301 [N_Axis]
  Refine = true
  Suppressed = false
  Type = 0
FEATURE [Sketcher::SketchObject] Sketch316
  ArcFitTolerance = 1e-06
  AttachmentSupport = -> [Pocket085]
  ExternalGeometry = -> [Pocket085]
  FullyConstrained = true
  MakeInternals = false
  MapMode = 5
  Placement = pos=(19.8,0,1.873e-13) rot=(0.57735,0.57735,0.57735;2.0944rad)
  sketch-geometry (10):
    g0: ArcOfCircle CenterX=-29.35 CenterY=-4 CenterZ=0 NormalX=0 NormalY=0 NormalZ=1 AngleXU=0 Radius=2.2 StartAngle=4.71239 EndAngle=6.28319
    g1: ArcOfCircle CenterX=-48.25 CenterY=-4 CenterZ=0 NormalX=0 NormalY=0 NormalZ=1 AngleXU=0 Radius=2.2 StartAngle=3.14159 EndAngle=4.71239
    g2: LineSegment StartX=-48.25 StartY=-6.2 StartZ=0 EndX=-29.35 EndY=-6.2 EndZ=0
    g3: LineSegment StartX=-27.15 StartY=-4 StartZ=0 EndX=-27.35 EndY=-4 EndZ=0
    g4: ArcOfCircle CenterX=-29.35 CenterY=-4 CenterZ=0 NormalX=0 NormalY=0 NormalZ=1 AngleXU=0 Radius=2 StartAngle=4.71239 EndAngle=6.28319
    g5: LineSegment StartX=-50.45 StartY=-4 StartZ=0 EndX=-50.25 EndY=-4 EndZ=0
    g6: ArcOfCircle CenterX=-48.25 CenterY=-4 CenterZ=0 NormalX=0 NormalY=0 NormalZ=1 AngleXU=0 Radius=2 StartAngle=3.14159 EndAngle=4.71239
    g7: LineSegment StartX=-48.25 StartY=-6 StartZ=0 EndX=-29.35 EndY=-6 EndZ=0
    g8: LineSegment [constr] StartX=-29.35 StartY=-6 StartZ=0 EndX=-29.35 EndY=-6.2 EndZ=0
    g9: LineSegment [constr] StartX=-48.25 StartY=-6 StartZ=0 EndX=-48.25 EndY=-6.2 EndZ=0
  constraints (26):
    c: Tangent(g0,g-5) = -1.5708
    c: Coincident(g0,g-5)
    c: Tangent(g1,g-3) = -1.5708
    c: Coincident(g1,g-4)
    c: Coincident(g2,g1)
    c: Coincident(g2,g0)
    c: Coincident(g3,g0)
    c: Horizontal(g3)
    c: Coincident(g4,g3)
    c: Coincident(g5,g1)
    c: Horizontal(g5)
    c: Coincident(g6,g5)
    c: Coincident(g7,g6)
    c: Coincident(g7,g4)
    c: Horizontal(g7)
    c: DistanceX(g5,g5) = 0.2
    c: Radius(g6) = 2
    c: Radius(g4) = 2
    c: Coincident(g8,g4)
    c: Coincident(g8,g0)
    c: Vertical(g8)
    c: Coincident(g9,g6)
    c: Coincident(g9,g1)
    c: Vertical(g9)
    c: DistanceY(g9,g9) = 0.2
    c: DistanceX(g3,g3) = 0.2
FEATURE [PartDesign::Pad] Pad211
  BaseFeature = -> Pocket085
  Direction = (1,1e-16,9.4e-15)
  Length = 1.7
  Length2 = 10
  Profile = -> Sketch316
  ReferenceAxis = -> Sketch316 [N_Axis]
  Refine = true
  Reversed = true
  Suppressed = false
  Type = 0
FEATURE [Sketcher::SketchObject] Sketch317
  ArcFitTolerance = 1e-06
  AttachmentSupport = -> [Pad211]
  ExternalGeometry = -> [Pad211]
  FullyConstrained = true
  MakeInternals = false
  MapMode = 5
  Placement = pos=(2.2,0,2.08e-14) rot=(0.57735,-0.57735,-0.57735;2.0944rad)
  sketch-geometry (8):
    g0: LineSegment StartX=27.15 StartY=-4 StartZ=0 EndX=27.35 EndY=-4 EndZ=0
    g1: LineSegment StartX=29.35 StartY=-6 StartZ=0 EndX=48.25 EndY=-6 EndZ=0
    g2: LineSegment StartX=48.25 StartY=-6.2 StartZ=0 EndX=29.35 EndY=-6.2 EndZ=0
    g3: ArcOfCircle CenterX=29.35 CenterY=-3.99999 CenterZ=0 NormalX=0 NormalY=0 NormalZ=1 AngleXU=0 Radius=2.00001 StartAngle=3.1416 EndAngle=4.71239
    g4: ArcOfCircle CenterX=29.35 CenterY=-4.00001 CenterZ=0 NormalX=0 NormalY=0 NormalZ=1 AngleXU=0 Radius=2.19999 StartAngle=3.14159 EndAngle=4.71239
    g5: LineSegment StartX=50.45 StartY=-4 StartZ=0 EndX=50.25 EndY=-4 EndZ=0
    g6: ArcOfCircle CenterX=48.25 CenterY=-3.99999 CenterZ=0 NormalX=0 NormalY=0 NormalZ=1 AngleXU=0 Radius=2.20001 StartAngle=4.71239 EndAngle=6.28318
    g7: ArcOfCircle CenterX=48.25 CenterY=-4 CenterZ=0 NormalX=0 NormalY=0 NormalZ=1 AngleXU=0 Radius=2 StartAngle=4.71239 EndAngle=6.28319
  constraints (20):
    c: Coincident(g0,g-3)
    c: Coincident(g0,g-6)
    c: Coincident(g1,g-8)
    c: Coincident(g1,g-7)
    c: Coincident(g3,g1)
    c: Coincident(g3,g0)
    c: Tangent(g3,g-6)
    c: Coincident(g4,g0)
    c: Coincident(g4,g2)
    c: Coincident(g2,g-4)
    c: Tangent(g4,g-3)
    c: Coincident(g5,g-5)
    c: Coincident(g5,g-8)
    c: Coincident(g6,g2)
    c: Coincident(g6,g5)
    c: Coincident(g2,g-5)
    c: Tangent(g6,g-5)
    c: Coincident(g7,g5)
    c: Coincident(g7,g1)
    c: Radius(g7) = 2
FEATURE [PartDesign::Pad] Pad212
  BaseFeature = -> Pad211
  Direction = (-1,1e-16,-9.4e-15)
  Length = 1.7
  Length2 = 10
  Profile = -> Sketch317
  ReferenceAxis = -> Sketch317 [N_Axis]
  Refine = true
  Reversed = true
  Suppressed = false
  Type = 0
FEATURE [Sketcher::SketchObject] Sketch321
  ArcFitTolerance = 1e-06
  AttachmentSupport = -> [Pad212]
  ExternalGeometry = -> [Pad212]
  FullyConstrained = true
  MakeInternals = false
  MapMode = 5
  Placement = pos=(19.8,0,1.618e-13) rot=(0.57735,0.57735,0.57735;2.0944rad)
  sketch-geometry (4):
    g0: LineSegment StartX=-50.25 StartY=-4 StartZ=0 EndX=-50.75 EndY=-4 EndZ=0
    g1: LineSegment StartX=-48.25 StartY=-6 StartZ=0 EndX=-48.75 EndY=-6 EndZ=0
    g2: ArcOfCircle CenterX=-48.75 CenterY=-4 CenterZ=0 NormalX=0 NormalY=0 NormalZ=1 AngleXU=0 Radius=2 StartAngle=3.14159 EndAngle=4.71239
    g3: ArcOfCircle CenterX=-48.25 CenterY=-4 CenterZ=0 NormalX=0 NormalY=0 NormalZ=1 AngleXU=0 Radius=2 StartAngle=3.14159 EndAngle=4.71239
  constraints (12):
    c: Coincident(g0,g-4)
    c: PointOnObject(g0,g-3)
    c: Coincident(g2,g0)
    c: Coincident(g2,g1)
    c: DistanceX(g0,g0) = 0.5
    c: DistanceX(g1,g1) = 0.5
    c: Coincident(g1,g-4)
    c: Horizontal(g1)
    c: PointOnObject(g2,g-5)
    c: Coincident(g3,g0)
    c: Coincident(g3,g1)
    c: Radius(g3) = 2
FEATURE [PartDesign::Pocket] Pocket223
  BaseFeature = -> Pad212
  Direction = (-1,-1e-16,-8.1e-15)
  Length = 3
  Length2 = 5
  Profile = -> Sketch321
  ReferenceAxis = -> Sketch321 [N_Axis]
  Refine = true
  Suppressed = false
  Type = 0
FEATURE [Sketcher::SketchObject] Sketch322
  ArcFitTolerance = 1e-06
  AttachmentSupport = -> [Pocket223]
  ExternalGeometry = -> [Pocket223]
  FullyConstrained = true
  MakeInternals = false
  MapMode = 5
  Placement = pos=(2.2,0,2.26e-14) rot=(0.57735,-0.57735,-0.57735;2.0944rad)
  sketch-geometry (4):
    g0: ArcOfCircle CenterX=48.25 CenterY=-4 CenterZ=0 NormalX=0 NormalY=0 NormalZ=1 AngleXU=0 Radius=2 StartAngle=4.71239 EndAngle=6.28319
    g1: ArcOfCircle CenterX=48.75 CenterY=-4 CenterZ=0 NormalX=0 NormalY=0 NormalZ=1 AngleXU=0 Radius=2 StartAngle=4.71239 EndAngle=6.28319
    g2: LineSegment StartX=50.75 StartY=-4 StartZ=0 EndX=50.25 EndY=-4 EndZ=0
    g3: LineSegment StartX=48.75 StartY=-6 StartZ=0 EndX=48.25 EndY=-6 EndZ=0
  constraints (8):
    c: Tangent(g0,g-3) = -1.5708
    c: Coincident(g0,g-3)
    c: Tangent(g1,g-5) = -1.5708
    c: Coincident(g1,g-5)
    c: Coincident(g2,g1)
    c: Coincident(g2,g0)
    c: Coincident(g3,g1)
    c: Coincident(g3,g0)
FEATURE [PartDesign::Pocket] Pocket224
  BaseFeature = -> Pocket223
  Direction = (1,0,1.02e-14)
  Length = 3
  Length2 = 5
  Profile = -> Sketch322
  ReferenceAxis = -> Sketch322 [N_Axis]
  Refine = true
  Suppressed = false
  Type = 0
FEATURE [PartDesign::Body] Body005  label="Front Legs"
  AllowCompound = false
  Group = -> [Binder001,Sketch057,Pad054,Sketch058,Pad055,Sketch059,Pocket023,Sketch060,Pocket024,Sketch061,Pad056,Sketch062,Pad057,Sketch063,Pocket025,Fillet031,Sketch064,Pocket026,Sketch065,Pocket027,Sketch066,Pocket028,Sketch067,Pocket029,Sketch068,Pocket030,Sketch069,Pocket031,Sketch070,Pocket032,Sketch187,Pad137,Sketch301,Pocket085,Sketch316,Pad211,Sketch317,Pad212,Sketch321,Pocket223,Sketch322,Pocket224,+15 more]
  Origin = -> Origin006
  Placement = pos=(33,20.95,0) rot=(0,0,1;0rad)
  Tip = -> Pocket243
COMPONENT P5 — recipe-attached ("Right_Shoulder", modeled in this document).
Construction recipe (the document's own serialized feature program — sketch geometry with constraints, then the solid features built on it; lengths are millimeters unless a unit is written):

FEATURE [Sketcher::SketchObject] Sketch137
  ArcFitTolerance = 1e-06
  AttachmentSupport = -> [XY_Plane016]
  FullyConstrained = true
  MakeInternals = false
  MapMode = 5
  sketch-geometry (8):
    g0: LineSegment StartX=-3.15 StartY=3.2 StartZ=0 EndX=-3.15 EndY=-3.2 EndZ=0
    g1: LineSegment StartX=-3.15 StartY=-3.2 StartZ=0 EndX=3.15 EndY=-3.2 EndZ=0
    g2: LineSegment StartX=3.15 StartY=-3.2 StartZ=0 EndX=3.15 EndY=1.2 EndZ=0
    g3: LineSegment StartX=3.15 StartY=1.2 StartZ=0 EndX=-0.35 EndY=1.2 EndZ=0
    g4: LineSegment StartX=-0.35 StartY=1.2 StartZ=0 EndX=-0.35 EndY=2.2 EndZ=0
    g5: LineSegment StartX=-0.35 StartY=2.2 StartZ=0 EndX=3.15 EndY=2.2 EndZ=0
    g6: LineSegment StartX=3.15 StartY=2.2 StartZ=0 EndX=3.15 EndY=3.2 EndZ=0
    g7: LineSegment StartX=3.15 StartY=3.2 StartZ=0 EndX=-3.15 EndY=3.2 EndZ=0
  constraints (24):
    c: Vertical(g0)
    c: Coincident(g1,g0)
    c: Horizontal(g1)
    c: Coincident(g2,g1)
    c: Vertical(g2)
    c: Coincident(g3,g2)
    c: Horizontal(g3)
    c: Coincident(g4,g3)
    c: Vertical(g4)
    c: Coincident(g5,g4)
    c: Horizontal(g5)
    c: Coincident(g6,g5)
    c: Vertical(g6)
    c: Horizontal(g7)
    c: Coincident(g0,g7)
    c: Coincident(g7,g6)
    c: DistanceY(g0,g0) = 6.4
    c: DistanceX(g1,g1) = 6.3
    c: DistanceY(g6,g6) = 1
    c: DistanceY(g4,g4) = 1
    c: DistanceX(g7,g7) = 6.3
    c: DistanceX(g3,g3) = 3.5
    c: DistanceX(g0,g-1) = 3.15
    c: DistanceY(g0,g-1) = 3.2
FEATURE [PartDesign::Pad] Pad111
  Direction = (0,0,1)
  Length = 8
  Length2 = 10
  Profile = -> Sketch137
  ReferenceAxis = -> Sketch137 [N_Axis]
  Refine = true
  Suppressed = false
  Type = 0
FEATURE [Sketcher::SketchObject] Sketch138
  ArcFitTolerance = 1e-06
  AttachmentSupport = -> [Pad111]
  ExternalGeometry = -> [Pad111]
  FullyConstrained = true
  MakeInternals = false
  MapMode = 5
  Placement = pos=(0,3.2,0) rot=(0,0.707107,0.707107;3.14159rad)
  sketch-geometry (8):
    g0: LineSegment StartX=-2.5 StartY=6.5 StartZ=0 EndX=-2.5 EndY=1.5 EndZ=0
    g1: LineSegment StartX=-2.5 StartY=1.5 StartZ=0 EndX=-1 EndY=1.5 EndZ=0
    g2: LineSegment StartX=-1 StartY=1.5 StartZ=0 EndX=-1 EndY=6.5 EndZ=0
    g3: LineSegment StartX=-1 StartY=6.5 StartZ=0 EndX=-2.5 EndY=6.5 EndZ=0
    g4: LineSegment StartX=1 StartY=6.5 StartZ=0 EndX=1 EndY=1.5 EndZ=0
    g5: LineSegment StartX=1 StartY=1.5 StartZ=0 EndX=2.5 EndY=1.5 EndZ=0
    g6: LineSegment StartX=2.5 StartY=1.5 StartZ=0 EndX=2.5 EndY=6.5 EndZ=0
    g7: LineSegment StartX=2.5 StartY=6.5 StartZ=0 EndX=1 EndY=6.5 EndZ=0
  constraints (26):
    c: Coincident(g0,g1)
    c: Coincident(g1,g2)
    c: Coincident(g2,g3)
    c: Coincident(g3,g0)
    c: Vertical(g0)
    c: Vertical(g2)
    c: Horizontal(g1)
    c: Horizontal(g3)
    c: Coincident(g4,g5)
    c: Coincident(g5,g6)
    c: Coincident(g6,g7)
    c: Coincident(g7,g4)
    c: Vertical(g4)
    c: Vertical(g6)
    c: Horizontal(g5)
    c: Horizontal(g7)
    c: DistanceX(g1,g1) = 1.5
    c: DistanceX(g5,g5) = 1.5
    c: DistanceY(g0,g0) = 5
    c: DistanceY(g4,g4) = 5
    c: DistanceX(g-3,g-3) = 6.3
    c: DistanceX(g1,g-1) = 1
    c: DistanceX(g-1,g4) = 1
    c: DistanceY(g-4,g-4) = 8
    c: DistanceY(g-4,g5) = 1.5
    c: DistanceY(g-3,g0) = 1.5
FEATURE [PartDesign::Pad] Pad112
  BaseFeature = -> Pad111
  Direction = (0,1,-2e-16)
  Length = 0.6
  Length2 = 10
  Profile = -> Sketch138
  ReferenceAxis = -> Sketch138 [N_Axis]
  Refine = true
  Suppressed = false
  Type = 0
FEATURE [Sketcher::SketchObject] Sketch139
  ArcFitTolerance = 1e-06
  AttachmentSupport = -> [Pad112]
  ExternalGeometry = -> [Pad112]
  FullyConstrained = true
  MakeInternals = false
  MapMode = 5
  Placement = pos=(0,-3.2,0) rot=(1,0,0;1.5708rad)
  sketch-geometry (4):
    g0: LineSegment StartX=3.15 StartY=6 StartZ=0 EndX=0.15 EndY=6 EndZ=0
    g1: LineSegment StartX=0.15 StartY=6 StartZ=0 EndX=0.15 EndY=2 EndZ=0
    g2: LineSegment StartX=0.15 StartY=2 StartZ=0 EndX=3.15 EndY=2 EndZ=0
    g3: LineSegment StartX=3.15 StartY=2 StartZ=0 EndX=3.15 EndY=6 EndZ=0
  constraints (12):
    c: Coincident(g0,g1)
    c: Coincident(g1,g2)
    c: Coincident(g2,g3)
    c: Coincident(g3,g0)
    c: Horizontal(g0)
    c: Horizontal(g2)
    c: Vertical(g1)
    c: Vertical(g3)
    c: PointOnObject(g0,g-3)
    c: DistanceY(g-3,g2) = 2
    c: DistanceY(g0,g-3) = 2
    c: DistanceX(g0,g0) = 3
FEATURE [PartDesign::Pad] Pad113
  BaseFeature = -> Pad112
  Direction = (0,-1,2e-16)
  Length = 2
  Length2 = 10
  Profile = -> Sketch139
  ReferenceAxis = -> Sketch139 [N_Axis]
  Refine = true
  Suppressed = false
  Type = 0
FEATURE [Sketcher::SketchObject] Sketch140
  ArcFitTolerance = 1e-06
  AttachmentSupport = -> [Pad113]
  ExternalGeometry = -> [Pad113]
  FullyConstrained = true
  MakeInternals = false
  MapMode = 5
  Placement = pos=(-3.15,0,0) rot=(0.57735,-0.57735,-0.57735;2.0944rad)
  sketch-geometry (1):
    g0: Circle CenterX=0 CenterY=4 CenterZ=0 NormalX=0 NormalY=0 NormalZ=1 AngleXU=0 Radius=0.9
  constraints (4):
    c: PointOnObject(g0,g-2)
    c: Diameter(g0) = 1.8
    c: DistanceY(g-3,g-3) = 8
    c: DistanceY(g-1,g0) = 4
FEATURE [PartDesign::Pocket] Pocket129
  BaseFeature = -> Pad113
  Direction = (1,0,0)
  Length = 7
  Length2 = 5
  Profile = -> Sketch140
  ReferenceAxis = -> Sketch140 [N_Axis]
  Refine = true
  Suppressed = false
  Type = 0
FEATURE [PartDesign::Body] Body014  label="Right_Shoulder"
  AllowCompound = false
  Group = -> [Sketch137,Pad111,Sketch138,Pad112,Sketch139,Pad113,Sketch140,Pocket129]
  Origin = -> Origin016
  Placement = pos=(47.15,20.2,-9) rot=(0,0,1;0rad)
  Tip = -> Pocket129
